FCSTD DOCUMENT  (FreeCAD 1.0R39319 (Git))
Label: Assembly_Launch-Monitor
License: All rights reserved
LicenseURL: https://en.wikipedia.org/wiki/All_rights_reserved
objects: App::Link×37, App::FeaturePython×13, Assembly::AssemblyLink×10, Assembly::JointGroup×1, Assembly::AssemblyObject×1
EXTERNAL_REF file=Assembly_PSU-Stack.FCStd obj=Assembly
EXTERNAL_REF file=Assembly_PSU-Stack.FCStd obj=Stack_Module_PSU
EXTERNAL_REF file=Assembly_PSU-Stack.FCStd obj=Ambient_LED_Screen
EXTERNAL_REF file=Assembly_PSU-Stack.FCStd obj=LinePower_Cover
EXTERNAL_REF file=Assembly_PSU-Stack.FCStd obj=Foot
EXTERNAL_REF file=Assembly_PSU-Stack.FCStd obj=Foot001
EXTERNAL_REF file=Assembly_PSU-Stack.FCStd obj=Foot002
EXTERNAL_REF file=Assembly_PSU-Stack.FCStd obj=Foot003
EXTERNAL_REF file=Assembly_PSU-Stack.FCStd obj=Spacer
EXTERNAL_REF file=Assembly_PSU-Stack.FCStd obj=Spacer001
EXTERNAL_REF file=Assembly_PSU-Stack.FCStd obj=Spacer002
EXTERNAL_REF file=Assembly_PSU-Stack.FCStd obj=Spacer003
EXTERNAL_REF file=Assembly_Flight-Cam-Stack.FCStd obj=Assembly
EXTERNAL_REF file=Assembly_Flight-Cam-Stack.FCStd obj=Stack_Module
EXTERNAL_REF file=Assembly_Flight-Cam-Stack.FCStd obj=Assembly_Flight_Cam_Screen
EXTERNAL_REF file=Assembly_Flight-Cam-Screen.FCStd obj=EyeScreen
EXTERNAL_REF file=Assembly_Flight-Cam-Screen.FCStd obj=EyeScreen_Clamp
EXTERNAL_REF file=Assembly_Flight-Cam-Screen.FCStd obj=Assembly_Flight_Cam
EXTERNAL_REF file=Assembly_Flight-Cam.FCStd obj=IMX296_MPI_Eyeball_6mm001
EXTERNAL_REF file=Assembly_Flight-Cam-Stack.FCStd obj=Spacer
EXTERNAL_REF file=Assembly_Flight-Cam-Stack.FCStd obj=Spacer001
EXTERNAL_REF file=Assembly_Flight-Cam-Stack.FCStd obj=Spacer002
EXTERNAL_REF file=Assembly_Flight-Cam-Stack.FCStd obj=Spacer003
EXTERNAL_REF file=Assembly_LED-Stack.FCStd obj=Assembly
EXTERNAL_REF file=Assembly_LED-Stack.FCStd obj=Stack_Module001
EXTERNAL_REF file=Assembly_LED-Stack.FCStd obj=Assembly_LED_Screen
EXTERNAL_REF file=Assembly_LED-Screen.FCStd obj=EyeScreen001
EXTERNAL_REF file=Assembly_LED-Screen.FCStd obj=Assembly_LED
EXTERNAL_REF file=Assembly_LED.FCStd obj=LED_Eyeball001
EXTERNAL_REF file=Assembly_LED.FCStd obj=LED_Clamp001
EXTERNAL_REF file=Assembly_LED-Screen.FCStd obj=EyeScreen_Clamp001
EXTERNAL_REF file=Assembly_LED-Stack.FCStd obj=Spacer001
EXTERNAL_REF file=Assembly_LED-Stack.FCStd obj=Spacer002
EXTERNAL_REF file=Assembly_LED-Stack.FCStd obj=Spacer003
EXTERNAL_REF file=Assembly_LED-Stack.FCStd obj=Spacer004
EXTERNAL_REF file=Assembly_Tee-Cam-Stack.FCStd obj=Assembly
EXTERNAL_REF file=Assembly_Tee-Cam-Stack.FCStd obj=Stack_Module
EXTERNAL_REF file=Assembly_Tee-Cam-Stack.FCStd obj=Spacer
EXTERNAL_REF file=Assembly_Tee-Cam-Stack.FCStd obj=Spacer001
EXTERNAL_REF file=Assembly_Tee-Cam-Stack.FCStd obj=Spacer002
EXTERNAL_REF file=Assembly_Tee-Cam-Stack.FCStd obj=Spacer003
EXTERNAL_REF file=Assembly_Tee-Cam-Stack.FCStd obj=Assembly_Tee_Cam_Screen
EXTERNAL_REF file=Assembly_Tee-Cam-Screen.FCStd obj=EyeScreen
EXTERNAL_REF file=Assembly_Tee-Cam-Screen.FCStd obj=EyeScreen_Clamp
EXTERNAL_REF file=Assembly_Tee-Cam-Screen.FCStd obj=Assembly_Tee_Cam
EXTERNAL_REF file=Assembly_Tee-Cam.FCStd obj=IMX296_MPI_Eyeball_6mm001
EXTERNAL_REF file=../Part/Print/Stack_Module_Cover.FCStd obj=Part

FEATURE [App::Link] Stack_Module_PSU
  LinkedObject = -> <external Assembly_PSU-Stack.FCStd>#Stack_Module_PSU
FEATURE [App::Link] Ambient_LED_Screen
  LinkPlacement = pos=(-1.22e-14,-3,-62.5) rot=(0,0.707107,-0.707107;3.14159rad)
  LinkedObject = -> <external Assembly_PSU-Stack.FCStd>#Ambient_LED_Screen
  Placement = pos=(-1.22e-14,-3,-62.5) rot=(0,0.707107,-0.707107;3.14159rad)
FEATURE [App::Link] LinePower_Cover
  LinkPlacement = pos=(56,-4,67) rot=(0,-0.707107,0.707107;3.14159rad)
  LinkedObject = -> <external Assembly_PSU-Stack.FCStd>#LinePower_Cover
  Placement = pos=(56,-4,67) rot=(0,-0.707107,0.707107;3.14159rad)
FEATURE [App::Link] Foot
  LinkPlacement = pos=(-66.5,5,-53.5) rot=(0.57735,-0.57735,0.57735;2.0944rad)
  LinkedObject = -> <external Assembly_PSU-Stack.FCStd>#Foot
  Placement = pos=(-66.5,5,-53.5) rot=(0.57735,-0.57735,0.57735;2.0944rad)
FEATURE [App::Link] Foot001
  LinkPlacement = pos=(-63.5,5,62.5) rot=(0.57735,-0.57735,0.57735;2.0944rad)
  LinkedObject = -> <external Assembly_PSU-Stack.FCStd>#Foot001
  Placement = pos=(-63.5,5,62.5) rot=(0.57735,-0.57735,0.57735;2.0944rad)
FEATURE [App::Link] Foot002
  LinkPlacement = pos=(66.5,5,-53.5) rot=(1,0,0;1.5708rad)
  LinkedObject = -> <external Assembly_PSU-Stack.FCStd>#Foot002
  Placement = pos=(66.5,5,-53.5) rot=(1,0,0;1.5708rad)
FEATURE [App::Link] Foot003
  LinkPlacement = pos=(63.5,5,62.5) rot=(0.57735,-0.57735,0.57735;2.0944rad)
  LinkedObject = -> <external Assembly_PSU-Stack.FCStd>#Foot003
  Placement = pos=(63.5,5,62.5) rot=(0.57735,-0.57735,0.57735;2.0944rad)
FEATURE [App::Link] Spacer
  LinkPlacement = pos=(66.5,-35.25,-53.5) rot=(-0.57735,0.57735,-0.57735;4.18879rad)
  LinkedObject = -> <external Assembly_PSU-Stack.FCStd>#Spacer
  Placement = pos=(66.5,-35.25,-53.5) rot=(-0.57735,0.57735,-0.57735;4.18879rad)
FEATURE [App::Link] Spacer001
  LinkPlacement = pos=(63.5,-35.25,62.5) rot=(-0.57735,0.57735,-0.57735;4.18879rad)
  LinkedObject = -> <external Assembly_PSU-Stack.FCStd>#Spacer001
  Placement = pos=(63.5,-35.25,62.5) rot=(-0.57735,0.57735,-0.57735;4.18879rad)
FEATURE [App::Link] Spacer002
  LinkPlacement = pos=(-66.5,-35.25,-53.5) rot=(-0.57735,0.57735,-0.57735;4.18879rad)
  LinkedObject = -> <external Assembly_PSU-Stack.FCStd>#Spacer002
  Placement = pos=(-66.5,-35.25,-53.5) rot=(-0.57735,0.57735,-0.57735;4.18879rad)
FEATURE [App::Link] Spacer003
  LinkPlacement = pos=(-63.5,-35.25,62.5) rot=(0.57735,-0.57735,0.57735;2.0944rad)
  LinkedObject = -> <external Assembly_PSU-Stack.FCStd>#Spacer003
  Placement = pos=(-63.5,-35.25,62.5) rot=(0.57735,-0.57735,0.57735;2.0944rad)
FEATURE [Assembly::AssemblyLink] Assembly_PSU_Stack  label="Assembly_PSU-Stack"
  Group = -> [Stack_Module_PSU,Ambient_LED_Screen,LinePower_Cover,Foot,Foot001,Foot002,Foot003,Spacer,Spacer001,Spacer002,Spacer003]
  LinkedObject = -> <external Assembly_PSU-Stack.FCStd>#Assembly
  Origin = -> Origin001
  Rigid = true
FEATURE [App::FeaturePython] GroundedJoint  # Assembly grounded joint (typed FeaturePython)
  ObjectToGround = -> Assembly_PSU_Stack
FEATURE [App::Link] Stack_Module
  LinkedObject = -> <external Assembly_Flight-Cam-Stack.FCStd>#Stack_Module
FEATURE [App::Link] EyeScreen
  LinkPlacement = pos=(0,0,0) rot=(0,0,1;3.14159rad)
  LinkedObject = -> <external Assembly_Flight-Cam-Screen.FCStd>#EyeScreen
  Placement = pos=(0,0,0) rot=(0,0,1;3.14159rad)
FEATURE [App::Link] EyeScreen_Clamp
  LinkPlacement = pos=(7.31e-14,1.49e-13,-3.757e-13) rot=(0,0,1;0rad)
  LinkedObject = -> <external Assembly_Flight-Cam-Screen.FCStd>#EyeScreen_Clamp
  Placement = pos=(7.31e-14,1.49e-13,-3.757e-13) rot=(0,0,1;0rad)
FEATURE [App::Link] IMX296_MPI_Eyeball_6mm001  label="IMX296-MPI_Eyeball_6mm001"
  LinkedObject = -> <external Assembly_Flight-Cam.FCStd>#IMX296_MPI_Eyeball_6mm001
FEATURE [Assembly::AssemblyLink] Assembly_Flight_Cam  label="Assembly_Flight-Cam"
  Group = -> [IMX296_MPI_Eyeball_6mm001]
  LinkedObject = -> <external Assembly_Flight-Cam-Screen.FCStd>#Assembly_Flight_Cam
  Placement = pos=(9.2e-15,0,0) rot=(0,-1,0;1.5708rad)
  Rigid = true
FEATURE [Assembly::AssemblyLink] Assembly_Flight_Cam_Screen  label="Assembly_Flight-Cam-Screen"
  Group = -> [EyeScreen,EyeScreen_Clamp,Assembly_Flight_Cam]
  LinkedObject = -> <external Assembly_Flight-Cam-Stack.FCStd>#Assembly_Flight_Cam_Screen
  Placement = pos=(-5.33e-14,-44.75,-20) rot=(0.57735,-0.57735,0.57735;2.0944rad)
  Rigid = true
FEATURE [App::Link] Spacer004
  LinkPlacement = pos=(-66.5,-82.5,-53.5) rot=(-0.57735,0.57735,-0.57735;4.18879rad)
  LinkedObject = -> <external Assembly_Flight-Cam-Stack.FCStd>#Spacer
  Placement = pos=(-66.5,-82.5,-53.5) rot=(-0.57735,0.57735,-0.57735;4.18879rad)
FEATURE [App::Link] Spacer005
  LinkPlacement = pos=(63.5,-82.5,62.5) rot=(-0.57735,0.57735,-0.57735;4.18879rad)
  LinkedObject = -> <external Assembly_Flight-Cam-Stack.FCStd>#Spacer001
  Placement = pos=(63.5,-82.5,62.5) rot=(-0.57735,0.57735,-0.57735;4.18879rad)
FEATURE [App::Link] Spacer006
  LinkPlacement = pos=(66.5,-82.5,-53.5) rot=(0.57735,-0.57735,0.57735;2.0944rad)
  LinkedObject = -> <external Assembly_Flight-Cam-Stack.FCStd>#Spacer002
  Placement = pos=(66.5,-82.5,-53.5) rot=(0.57735,-0.57735,0.57735;2.0944rad)
FEATURE [App::Link] Spacer007
  LinkPlacement = pos=(-63.5,-82.5,62.5) rot=(-0.57735,0.57735,-0.57735;4.18879rad)
  LinkedObject = -> <external Assembly_Flight-Cam-Stack.FCStd>#Spacer003
  Placement = pos=(-63.5,-82.5,62.5) rot=(-0.57735,0.57735,-0.57735;4.18879rad)
FEATURE [Assembly::AssemblyLink] Assembly_Flight_Cam_Stack  label="Assembly_Flight-Cam-Stack"
  Group = -> [Stack_Module,Assembly_Flight_Cam_Screen,Spacer004,Spacer005,Spacer006,Spacer007]
  LinkedObject = -> <external Assembly_Flight-Cam-Stack.FCStd>#Assembly
  Origin = -> Origin002
  Placement = pos=(-6.5e-15,-40.25,1.049e-13) rot=(0,0,1;0rad)
  Rigid = true
FEATURE [App::FeaturePython] Joint  label="Distance"  # Assembly joint (typed FeaturePython)
  Activated = true
  AngleMax = 0
  AngleMin = 0
  Detach1 = false
  Detach2 = false
  Distance = 0
  Distance2 = 0
  EnableAngleMax = false
  EnableAngleMin = false
  EnableLengthMax = false
  EnableLengthMin = false
  JointType = 5 (Distance)
  LengthMax = 0
  LengthMin = 0
  Placement1 = pos=(-6.7e-15,3.7e-15,-15.8114) rot=(-0.57735,0.57735,0.57735;2.0944rad)
  Placement2 = pos=(6.38556,-40.25,16.7734) rot=(-0.57735,0.57735,-0.57735;4.18879rad)
  Reference1 = -> Assembly [Assembly_Flight_Cam_Stack.Stack_Module.Body.Face88,Assembly_Flight_Cam_Stack.Stack_Module.Body.Vertex265]
  Reference2 = -> Assembly [Assembly_PSU_Stack.Stack_Module_PSU.Body.Face4,Assembly_PSU_Stack.Stack_Module_PSU.Body.Vertex81]
FEATURE [App::FeaturePython] Joint001  label="Distance001"  # Assembly joint (typed FeaturePython)
  Activated = true
  AngleMax = 0
  AngleMin = 0
  Detach1 = false
  Detach2 = false
  Distance = 0
  Distance2 = 0
  EnableAngleMax = false
  EnableAngleMin = false
  EnableLengthMax = false
  EnableLengthMin = false
  JointType = 5 (Distance)
  LengthMax = 0
  LengthMin = 0
  Placement1 = pos=(59,-20.125,4.65153) rot=(0,-1,0;1.5708rad)
  Placement2 = pos=(59,-43.75,4.65153) rot=(0,-1,0;1.5708rad)
  Reference1 = -> Assembly [Assembly_PSU_Stack.Stack_Module_PSU.Body.Face30,Assembly_PSU_Stack.Stack_Module_PSU.Body.Face30]
  Reference2 = -> Assembly [Assembly_Flight_Cam_Stack.Stack_Module.Body.Face23,Assembly_Flight_Cam_Stack.Stack_Module.Body.Face23]
FEATURE [App::FeaturePython] Joint002  label="Distance002"  # Assembly joint (typed FeaturePython)
  Activated = true
  AngleMax = 0
  AngleMin = 0
  Detach1 = false
  Detach2 = false
  Distance = 0
  Distance2 = 0
  EnableAngleMax = false
  EnableAngleMin = false
  EnableLengthMax = false
  EnableLengthMin = false
  JointType = 5 (Distance)
  LengthMax = 0
  LengthMin = 0
  Placement1 = pos=(-1.62e-14,-10.6176,-70) rot=(0.707107,0.707107,0;3.14159rad)
  Placement2 = pos=(71,-43.75,-70) rot=(-0.57735,-0.57735,0.57735;4.18879rad)
  Reference1 = -> Assembly [Assembly_PSU_Stack.Stack_Module_PSU.Body.Face39,Assembly_PSU_Stack.Stack_Module_PSU.Body.Vertex41]
  Reference2 = -> Assembly [Assembly_Flight_Cam_Stack.Stack_Module.Body.Edge101,Assembly_Flight_Cam_Stack.Stack_Module.Body.Vertex87]
FEATURE [App::Link] Stack_Module001
  LinkedObject = -> <external Assembly_LED-Stack.FCStd>#Stack_Module001
FEATURE [App::Link] EyeScreen001
  LinkedObject = -> <external Assembly_LED-Screen.FCStd>#EyeScreen001
FEATURE [App::Link] LED_Eyeball001
  LinkedObject = -> <external Assembly_LED.FCStd>#LED_Eyeball001
FEATURE [App::Link] LED_Clamp001
  LinkPlacement = pos=(3.8e-15,4.1e-15,-13.35) rot=(0,0,-1;0.785398rad)
  LinkedObject = -> <external Assembly_LED.FCStd>#LED_Clamp001
  Placement = pos=(3.8e-15,4.1e-15,-13.35) rot=(0,0,-1;0.785398rad)
FEATURE [Assembly::AssemblyLink] Assembly_LED
  Group = -> [LED_Eyeball001,LED_Clamp001]
  LinkedObject = -> <external Assembly_LED-Screen.FCStd>#Assembly_LED
  Placement = pos=(-9.2e-15,0,0) rot=(0.678598,0.281085,0.678598;2.59356rad)
  Rigid = true
FEATURE [App::Link] EyeScreen_Clamp001
  LinkPlacement = pos=(-8.42e-14,1.222e-13,2.46e-14) rot=(0,0,1;3.14159rad)
  LinkedObject = -> <external Assembly_LED-Screen.FCStd>#EyeScreen_Clamp001
  Placement = pos=(-8.42e-14,1.222e-13,2.46e-14) rot=(0,0,1;3.14159rad)
FEATURE [Assembly::AssemblyLink] Assembly_LED_Screen  label="Assembly_LED-Screen"
  Group = -> [EyeScreen001,Assembly_LED,EyeScreen_Clamp001]
  LinkedObject = -> <external Assembly_LED-Stack.FCStd>#Assembly_LED_Screen
  Placement = pos=(-2.02e-14,-44.75,-20) rot=(0.57735,0.57735,-0.57735;2.0944rad)
  Rigid = true
FEATURE [App::Link] Spacer008
  LinkPlacement = pos=(63.5,-82.5,62.5) rot=(0.57735,-0.57735,0.57735;2.0944rad)
  LinkedObject = -> <external Assembly_LED-Stack.FCStd>#Spacer001
  Placement = pos=(63.5,-82.5,62.5) rot=(0.57735,-0.57735,0.57735;2.0944rad)
FEATURE [App::Link] Spacer009
  LinkPlacement = pos=(66.5,-82.5,-53.5) rot=(-0.57735,0.57735,-0.57735;4.18879rad)
  LinkedObject = -> <external Assembly_LED-Stack.FCStd>#Spacer002
  Placement = pos=(66.5,-82.5,-53.5) rot=(-0.57735,0.57735,-0.57735;4.18879rad)
FEATURE [App::Link] Spacer010
  LinkPlacement = pos=(-66.5,-82.5,-53.5) rot=(-0.57735,0.57735,-0.57735;4.18879rad)
  LinkedObject = -> <external Assembly_LED-Stack.FCStd>#Spacer003
  Placement = pos=(-66.5,-82.5,-53.5) rot=(-0.57735,0.57735,-0.57735;4.18879rad)
FEATURE [App::Link] Spacer011
  LinkPlacement = pos=(-63.5,-82.5,62.5) rot=(-0.57735,0.57735,-0.57735;4.18879rad)
  LinkedObject = -> <external Assembly_LED-Stack.FCStd>#Spacer004
  Placement = pos=(-63.5,-82.5,62.5) rot=(-0.57735,0.57735,-0.57735;4.18879rad)
FEATURE [Assembly::AssemblyLink] Assembly_LED_Stack  label="Assembly_LED-Stack"
  Group = -> [Stack_Module001,Assembly_LED_Screen,Spacer008,Spacer009,Spacer010,Spacer011]
  LinkedObject = -> <external Assembly_LED-Stack.FCStd>#Assembly
  Origin = -> Origin003
  Placement = pos=(-8.5e-15,-127.75,1.504e-13) rot=(0,0,1;0rad)
  Rigid = true
FEATURE [App::FeaturePython] Joint003  label="Distance003"  # Assembly joint (typed FeaturePython)
  Activated = true
  AngleMax = 0
  AngleMin = 0
  Detach1 = false
  Detach2 = false
  Distance = 0
  Distance2 = 0
  EnableAngleMax = false
  EnableAngleMin = false
  EnableLengthMax = false
  EnableLengthMin = false
  JointType = 5 (Distance)
  LengthMax = 0
  LengthMin = 0
  Placement1 = pos=(-6.7e-15,3.7e-15,-15.8114) rot=(-0.57735,0.57735,0.57735;2.0944rad)
  Placement2 = pos=(57.7645,-87.5,-3.95134) rot=(0.57735,-0.57735,0.57735;2.0944rad)
  Reference1 = -> Assembly [Assembly_LED_Stack.Stack_Module001.Face88,Assembly_LED_Stack.Stack_Module001.Vertex296]
  Reference2 = -> Assembly [Assembly_Flight_Cam_Stack.Stack_Module.Body.Face52,Assembly_Flight_Cam_Stack.Stack_Module.Body.Vertex174]
FEATURE [App::FeaturePython] Joint004  label="Distance004"  # Assembly joint (typed FeaturePython)
  Activated = true
  AngleMax = 0
  AngleMin = 0
  Detach1 = false
  Detach2 = false
  Distance = 0
  Distance2 = 0
  EnableAngleMax = false
  EnableAngleMin = false
  EnableLengthMax = false
  EnableLengthMin = false
  JointType = 5 (Distance)
  LengthMax = 0
  LengthMin = 0
  Placement1 = pos=(59,-43.75,4.65153) rot=(0,-1,0;1.5708rad)
  Placement2 = pos=(59,-43.75,4.65153) rot=(0,-1,0;1.5708rad)
  Reference1 = -> Assembly [Assembly_LED_Stack.Stack_Module001.Face23,Assembly_LED_Stack.Stack_Module001.Face23]
  Reference2 = -> Assembly [Assembly_Flight_Cam_Stack.Stack_Module.Body.Face23,Assembly_Flight_Cam_Stack.Stack_Module.Body.Face23]
FEATURE [App::FeaturePython] Joint005  label="Distance005"  # Assembly joint (typed FeaturePython)
  Activated = true
  AngleMax = 0
  AngleMin = 0
  Detach1 = false
  Detach2 = false
  Distance = 0
  Distance2 = 0
  EnableAngleMax = false
  EnableAngleMin = false
  EnableLengthMax = false
  EnableLengthMin = false
  JointType = 5 (Distance)
  LengthMax = 0
  LengthMin = 0
  Placement1 = pos=(68,-43.75,-70) rot=(0,0,1;0rad)
  Placement2 = pos=(68,-43.75,-70) rot=(0,0,1;0rad)
  Reference1 = -> Assembly [Assembly_LED_Stack.Stack_Module001.Face15,Assembly_LED_Stack.Stack_Module001.Vertex88]
  Reference2 = -> Assembly [Assembly_Flight_Cam_Stack.Stack_Module.Body.Face15,Assembly_Flight_Cam_Stack.Stack_Module.Body.Vertex90]
FEATURE [App::Link] Stack_Module002
  LinkedObject = -> <external Assembly_Tee-Cam-Stack.FCStd>#Stack_Module
FEATURE [App::Link] Spacer012
  LinkPlacement = pos=(-66.5,-82.5,-53.5) rot=(-0.57735,0.57735,-0.57735;4.18879rad)
  LinkedObject = -> <external Assembly_Tee-Cam-Stack.FCStd>#Spacer
  Placement = pos=(-66.5,-82.5,-53.5) rot=(-0.57735,0.57735,-0.57735;4.18879rad)
FEATURE [App::Link] Spacer013
  LinkPlacement = pos=(63.5,-82.5,62.5) rot=(0.57735,-0.57735,0.57735;2.0944rad)
  LinkedObject = -> <external Assembly_Tee-Cam-Stack.FCStd>#Spacer001
  Placement = pos=(63.5,-82.5,62.5) rot=(0.57735,-0.57735,0.57735;2.0944rad)
FEATURE [App::Link] Spacer014
  LinkPlacement = pos=(66.5,-82.5,-53.5) rot=(0.57735,-0.57735,0.57735;2.0944rad)
  LinkedObject = -> <external Assembly_Tee-Cam-Stack.FCStd>#Spacer002
  Placement = pos=(66.5,-82.5,-53.5) rot=(0.57735,-0.57735,0.57735;2.0944rad)
FEATURE [App::Link] Spacer015
  LinkPlacement = pos=(-63.5,-82.5,62.5) rot=(-0.57735,0.57735,-0.57735;4.18879rad)
  LinkedObject = -> <external Assembly_Tee-Cam-Stack.FCStd>#Spacer003
  Placement = pos=(-63.5,-82.5,62.5) rot=(-0.57735,0.57735,-0.57735;4.18879rad)
FEATURE [App::Link] EyeScreen002
  LinkPlacement = pos=(0,0,0) rot=(0,0,1;3.14159rad)
  LinkedObject = -> <external Assembly_Tee-Cam-Screen.FCStd>#EyeScreen
  Placement = pos=(0,0,0) rot=(0,0,1;3.14159rad)
FEATURE [App::Link] EyeScreen_Clamp002
  LinkPlacement = pos=(6.2e-14,1.473e-13,-3.4e-13) rot=(0,0,1;0rad)
  LinkedObject = -> <external Assembly_Tee-Cam-Screen.FCStd>#EyeScreen_Clamp
  Placement = pos=(6.2e-14,1.473e-13,-3.4e-13) rot=(0,0,1;0rad)
FEATURE [App::Link] IMX296_MPI_Eyeball_6mm002  label="IMX296-MPI_Eyeball_6mm002"
  LinkedObject = -> <external Assembly_Tee-Cam.FCStd>#IMX296_MPI_Eyeball_6mm001
FEATURE [Assembly::AssemblyLink] Assembly_Tee_Cam  label="Assembly_Tee-Cam"
  Group = -> [IMX296_MPI_Eyeball_6mm002]
  LinkedObject = -> <external Assembly_Tee-Cam-Screen.FCStd>#Assembly_Tee_Cam
  Placement = pos=(9.2e-15,0,0) rot=(0.57735,0.57735,-0.57735;4.18879rad)
  Rigid = true
FEATURE [Assembly::AssemblyLink] Assembly_Tee_Cam_Screen  label="Assembly_Tee-Cam-Screen"
  Group = -> [EyeScreen002,EyeScreen_Clamp002,Assembly_Tee_Cam]
  LinkedObject = -> <external Assembly_Tee-Cam-Stack.FCStd>#Assembly_Tee_Cam_Screen
  Placement = pos=(1,-44.75,-20) rot=(-0.57735,0.57735,-0.57735;4.18879rad)
  Rigid = true
FEATURE [Assembly::AssemblyLink] Assembly_Tee_Cam_Stack  label="Assembly_Tee-Cam-Stack"
  Group = -> [Stack_Module002,Spacer012,Spacer013,Spacer014,Spacer015,Assembly_Tee_Cam_Screen]
  LinkedObject = -> <external Assembly_Tee-Cam-Stack.FCStd>#Assembly
  Origin = -> Origin004
  Placement = pos=(-2.32e-14,-215.25,1.736e-13) rot=(0,0,1;0rad)
  Rigid = true
FEATURE [App::FeaturePython] Joint006  label="Distance006"  # Assembly joint (typed FeaturePython)
  Activated = true
  AngleMax = 0
  AngleMin = 0
  Detach1 = false
  Detach2 = false
  Distance = 0
  Distance2 = 0
  EnableAngleMax = false
  EnableAngleMin = false
  EnableLengthMax = false
  EnableLengthMin = false
  JointType = 5 (Distance)
  LengthMax = 0
  LengthMin = 0
  Placement1 = pos=(-6.7e-15,3.7e-15,-15.8114) rot=(-0.57735,0.57735,0.57735;2.0944rad)
  Placement2 = pos=(-57.7645,-87.5,-3.95134) rot=(0.57735,0.57735,0.57735;4.18879rad)
  Reference1 = -> Assembly [Assembly_Tee_Cam_Stack.Stack_Module002.Body.Face88,Assembly_Tee_Cam_Stack.Stack_Module002.Body.Vertex258]
  Reference2 = -> Assembly [Assembly_LED_Stack.Stack_Module001.Face131,Assembly_LED_Stack.Stack_Module001.Vertex351]
FEATURE [App::FeaturePython] Joint007  label="Distance007"  # Assembly joint (typed FeaturePython)
  Activated = true
  AngleMax = 0
  AngleMin = 0
  Detach1 = false
  Detach2 = false
  Distance = 0
  Distance2 = 0
  EnableAngleMax = false
  EnableAngleMin = false
  EnableLengthMax = false
  EnableLengthMin = false
  JointType = 5 (Distance)
  LengthMax = 0
  LengthMin = 0
  Placement1 = pos=(59,-43.75,4.65153) rot=(0,-1,0;1.5708rad)
  Placement2 = pos=(59,-43.75,4.65153) rot=(0,-1,0;1.5708rad)
  Reference1 = -> Assembly [Assembly_Tee_Cam_Stack.Stack_Module002.Body.Face23,Assembly_Tee_Cam_Stack.Stack_Module002.Body.Face23]
  Reference2 = -> Assembly [Assembly_LED_Stack.Stack_Module001.Face23,Assembly_LED_Stack.Stack_Module001.Face23]
FEATURE [App::FeaturePython] Joint008  label="Distance008"  # Assembly joint (typed FeaturePython)
  Activated = true
  AngleMax = 0
  AngleMin = 0
  Detach1 = false
  Detach2 = false
  Distance = 0
  Distance2 = 0
  EnableAngleMax = false
  EnableAngleMin = false
  EnableLengthMax = false
  EnableLengthMin = false
  JointType = 5 (Distance)
  LengthMax = 0
  LengthMin = 0
  Placement1 = pos=(68,-43.75,-70) rot=(0,0,1;0rad)
  Placement2 = pos=(68,-43.75,-70) rot=(0,0,1;0rad)
  Reference1 = -> Assembly [Assembly_Tee_Cam_Stack.Stack_Module002.Body.Face15,Assembly_Tee_Cam_Stack.Stack_Module002.Body.Face15]
  Reference2 = -> Assembly [Assembly_LED_Stack.Stack_Module001.Face15,Assembly_LED_Stack.Stack_Module001.Vertex90]
FEATURE [App::Link] Stack_Module_Cover
  LinkPlacement = pos=(-5.16e-14,-302.75,3.692e-13) rot=(0,0,1;0rad)
  LinkedObject = -> <external ../Part/Print/Stack_Module_Cover.FCStd>#Part
  Placement = pos=(-5.16e-14,-302.75,3.692e-13) rot=(0,0,1;0rad)
FEATURE [App::FeaturePython] Joint009  label="Distance009"  # Assembly joint (typed FeaturePython)
  Activated = true
  AngleMax = 0
  AngleMin = 0
  Detach1 = false
  Detach2 = false
  Distance = 0
  Distance2 = 0
  EnableAngleMax = false
  EnableAngleMin = false
  EnableLengthMax = false
  EnableLengthMin = false
  JointType = 5 (Distance)
  LengthMax = 0
  LengthMin = 0
  Placement1 = pos=(-1.02e-14,8.7e-15,13.4612) rot=(-0.57735,0.57735,0.57735;2.0944rad)
  Placement2 = pos=(57.7645,-87.5,-3.95134) rot=(0.57735,-0.57735,0.57735;2.0944rad)
  Reference1 = -> Assembly [Stack_Module_Cover.Body.Face2,Stack_Module_Cover.Body.Vertex34]
  Reference2 = -> Assembly [Assembly_Tee_Cam_Stack.Stack_Module002.Body.Face52,Assembly_Tee_Cam_Stack.Stack_Module002.Body.Vertex174]
FEATURE [App::FeaturePython] Joint010  label="Distance010"  # Assembly joint (typed FeaturePython)
  Activated = true
  AngleMax = 0
  AngleMin = 0
  Detach1 = false
  Detach2 = false
  Distance = 0
  Distance2 = 0
  EnableAngleMax = false
  EnableAngleMin = false
  EnableLengthMax = false
  EnableLengthMin = false
  JointType = 5 (Distance)
  LengthMax = 0
  LengthMin = 0
  Placement1 = pos=(59,-5,4.65153) rot=(0,-1,0;1.5708rad)
  Placement2 = pos=(59,-43.75,4.65153) rot=(0,-1,0;1.5708rad)
  Reference1 = -> Assembly [Stack_Module_Cover.Body.Face16,Stack_Module_Cover.Body.Face16]
  Reference2 = -> Assembly [Assembly_Tee_Cam_Stack.Stack_Module002.Body.Face23,Assembly_Tee_Cam_Stack.Stack_Module002.Body.Face23]
FEATURE [App::FeaturePython] Joint011  label="Distance011"  # Assembly joint (typed FeaturePython)
  Activated = true
  AngleMax = 0
  AngleMin = 0
  Detach1 = false
  Detach2 = false
  Distance = 0
  Distance2 = 0
  EnableAngleMax = false
  EnableAngleMin = false
  EnableLengthMax = false
  EnableLengthMin = false
  JointType = 5 (Distance)
  LengthMax = 0
  LengthMin = 0
  Placement1 = pos=(0,-5.70149,-70) rot=(0.707107,0.707107,0;3.14159rad)
  Placement2 = pos=(68,-43.75,-70) rot=(0,0,1;0rad)
  Reference1 = -> Assembly [Stack_Module_Cover.Body.Face5,Stack_Module_Cover.Body.Vertex45]
  Reference2 = -> Assembly [Assembly_Tee_Cam_Stack.Stack_Module002.Body.Face15,Assembly_Tee_Cam_Stack.Stack_Module002.Body.Vertex90]
FEATURE [Assembly::JointGroup] Joints
  Group = -> [GroundedJoint,Joint,Joint001,Joint002,Joint003,Joint004,Joint005,Joint006,Joint007,Joint008,Joint009,Joint010,Joint011]
FEATURE [Assembly::AssemblyObject] Assembly  label="Assembly_Launch-Monitor"
  Group = -> [Joints,Assembly_PSU_Stack,GroundedJoint,Assembly_Flight_Cam_Stack,Joint,Joint001,Joint002,Assembly_LED_Stack,Joint003,Joint004,Joint005,Assembly_Tee_Cam_Stack,Joint006,Joint007,Joint008,Stack_Module_Cover,Joint009,Joint010,Joint011]
  Origin = -> Origin
  Type = Assembly

RESOLVED EXTERNAL PARTS (link-assembly join: the EXTERNAL_REF files above that resolve inside this repo's crawl, each included once):
---- part Assembly_Flight-Cam-Screen.FCStd = doc fcstd_e77e65b90301 ----
FCSTD DOCUMENT  (FreeCAD 1.0R39319 (Git))
Label: Assembly_Flight-Cam-Screen
License: All rights reserved
LicenseURL: https://en.wikipedia.org/wiki/All_rights_reserved
objects: App::FeaturePython×5, App::Link×3, Assembly::AssemblyLink×1, Assembly::JointGroup×1, Assembly::AssemblyObject×1
EXTERNAL_REF file=../Part/Print/EyeScreen.FCStd obj=Part
EXTERNAL_REF file=../Part/Print/EyeScreen_Clamp.FCStd obj=Part
EXTERNAL_REF file=Assembly_Flight-Cam.FCStd obj=Assembly
EXTERNAL_REF file=Assembly_Flight-Cam.FCStd obj=IMX296_MPI_Eyeball_6mm001

FEATURE [App::Link] EyeScreen
  LinkPlacement = pos=(0,0,0) rot=(0,0,1;3.14159rad)
  LinkedObject = -> <external ../Part/Print/EyeScreen.FCStd>#Part
  Placement = pos=(0,0,0) rot=(0,0,1;3.14159rad)
FEATURE [App::Link] EyeScreen_Clamp
  LinkPlacement = pos=(6.23e-14,1.5e-13,-2.196e-13) rot=(0,0,1;0rad)
  LinkedObject = -> <external ../Part/Print/EyeScreen_Clamp.FCStd>#Part
  Placement = pos=(6.23e-14,1.5e-13,-2.196e-13) rot=(0,0,1;0rad)
FEATURE [App::FeaturePython] GroundedJoint  # Assembly grounded joint (typed FeaturePython)
  ObjectToGround = -> EyeScreen
FEATURE [App::FeaturePython] Joint  label="Distance"  # Assembly joint (typed FeaturePython)
  Activated = true
  AngleMax = 0
  AngleMin = 0
  Detach1 = false
  Detach2 = false
  Distance = -1
  Distance2 = 0
  EnableAngleMax = false
  EnableAngleMin = false
  EnableLengthMax = false
  EnableLengthMin = false
  JointType = 5 (Distance)
  LengthMax = 0
  LengthMin = 0
  Placement1 = pos=(1,-2.077e-13,-1.63309) rot=(0.707107,0,0.707107;3.14159rad)
  Placement2 = pos=(4.82e-14,-4.807e-13,-1.66411) rot=(0.707107,0,-0.707107;3.14159rad)
  Reference1 = -> Assembly [EyeScreen_Clamp.Body.Face3,EyeScreen_Clamp.Body.Edge29]
  Reference2 = -> Assembly [EyeScreen.Body.Face105,EyeScreen.Body.Vertex111]
FEATURE [App::FeaturePython] Joint001  label="Cylindrical"  # Assembly joint (typed FeaturePython)
  Activated = true
  AngleMax = 0
  AngleMin = 0
  Detach1 = false
  Detach2 = false
  Distance = 0
  Distance2 = 0
  EnableAngleMax = false
  EnableAngleMin = false
  EnableLengthMax = false
  EnableLengthMin = false
  JointType = 2 (Cylindrical)
  LengthMax = 0
  LengthMin = 0
  Placement1 = pos=(3,-43.3013,25) rot=(0.57735,-0.57735,-0.57735;2.0944rad)
  Placement2 = pos=(5,43.3013,25) rot=(0.57735,0.57735,0.57735;2.0944rad)
  Reference1 = -> Assembly [EyeScreen_Clamp.Body.Face32,EyeScreen_Clamp.Body.Face32]
  Reference2 = -> Assembly [EyeScreen.Body.Face28,EyeScreen.Body.Face28]
FEATURE [App::FeaturePython] Joint002  label="Cylindrical001"  # Assembly joint (typed FeaturePython)
  Activated = true
  AngleMax = 0
  AngleMin = 0
  Detach1 = false
  Detach2 = false
  Distance = 0
  Distance2 = 0
  EnableAngleMax = false
  EnableAngleMin = false
  EnableLengthMax = false
  EnableLengthMin = false
  JointType = 2 (Cylindrical)
  LengthMax = 0
  LengthMin = 0
  Placement1 = pos=(3,-43.3013,-25) rot=(0.57735,-0.57735,0.57735;4.18879rad)
  Placement2 = pos=(5,43.3013,-25) rot=(0.57735,0.57735,-0.57735;4.18879rad)
  Reference1 = -> Assembly [EyeScreen_Clamp.Body.Face31,EyeScreen_Clamp.Body.Face31]
  Reference2 = -> Assembly [EyeScreen.Body.Face29,EyeScreen.Body.Face29]
FEATURE [App::Link] IMX296_MPI_Eyeball_6mm001  label="IMX296-MPI_Eyeball_6mm001"
  LinkedObject = -> <external Assembly_Flight-Cam.FCStd>#IMX296_MPI_Eyeball_6mm001
FEATURE [Assembly::AssemblyLink] Assembly_Flight_Cam  label="Assembly_Flight-Cam"
  Group = -> [IMX296_MPI_Eyeball_6mm001]
  LinkedObject = -> <external Assembly_Flight-Cam.FCStd>#Assembly
  Origin = -> Origin001
  Placement = pos=(9.2e-15,0,0) rot=(0,-1,0;1.5708rad)
  Rigid = true
FEATURE [App::FeaturePython] Joint003  label="Ball"  # Assembly joint (typed FeaturePython)
  Activated = true
  AngleMax = 0
  AngleMin = 0
  Detach1 = false
  Detach2 = false
  Distance = 0
  Distance2 = 0
  EnableAngleMax = false
  EnableAngleMin = false
  EnableLengthMax = false
  EnableLengthMin = false
  JointType = 4 (Ball)
  LengthMax = 0
  LengthMin = 0
  Placement1 = pos=(0,0,0) rot=(1,0,0;3.14159rad)
  Placement2 = pos=(-9.2e-15,0,0) rot=(0.707107,0,0.707107;3.14159rad)
  Reference1 = -> Assembly [Assembly_Flight_Cam.IMX296_MPI_Eyeball_6mm001.Face1,Assembly_Flight_Cam.IMX296_MPI_Eyeball_6mm001.Face1]
  Reference2 = -> Assembly [EyeScreen.Body.Edge142,EyeScreen.Body.Edge142]
FEATURE [Assembly::JointGroup] Joints
  Group = -> [GroundedJoint,Joint,Joint001,Joint002,Joint003]
FEATURE [Assembly::AssemblyObject] Assembly  label="Assembly_Flight-Cam-Screen"
  Group = -> [Joints,EyeScreen,EyeScreen_Clamp,GroundedJoint,Joint,Joint001,Joint002,Assembly_Flight_Cam,Joint003]
  Origin = -> Origin
  Type = Assembly_Flight-Cam-Screen
---- part Assembly_Flight-Cam-Stack.FCStd = doc fcstd_b05a0b03a1ce ----
FCSTD DOCUMENT  (FreeCAD 1.0R39319 (Git))
Label: Assembly_Flight-Cam-Stack
License: All rights reserved
LicenseURL: https://en.wikipedia.org/wiki/All_rights_reserved
objects: App::FeaturePython×12, App::Link×8, Assembly::AssemblyLink×2, Assembly::JointGroup×1, Assembly::AssemblyObject×1
EXTERNAL_REF file=../Part/Print/Stack_Module.FCStd obj=Part
EXTERNAL_REF file=Assembly_Flight-Cam-Screen.FCStd obj=Assembly
EXTERNAL_REF file=Assembly_Flight-Cam-Screen.FCStd obj=EyeScreen
EXTERNAL_REF file=Assembly_Flight-Cam-Screen.FCStd obj=EyeScreen_Clamp
EXTERNAL_REF file=Assembly_Flight-Cam-Screen.FCStd obj=Assembly_Flight_Cam
EXTERNAL_REF file=Assembly_Flight-Cam.FCStd obj=IMX296_MPI_Eyeball_6mm001
EXTERNAL_REF file=../Part/Print/Spacer.FCStd obj=Part

FEATURE [App::Link] Stack_Module
  LinkedObject = -> <external ../Part/Print/Stack_Module.FCStd>#Part
FEATURE [App::FeaturePython] GroundedJoint  # Assembly grounded joint (typed FeaturePython)
  ObjectToGround = -> Stack_Module
FEATURE [App::Link] EyeScreen
  LinkPlacement = pos=(0,0,0) rot=(0,0,1;3.14159rad)
  LinkedObject = -> <external Assembly_Flight-Cam-Screen.FCStd>#EyeScreen
  Placement = pos=(0,0,0) rot=(0,0,1;3.14159rad)
FEATURE [App::Link] EyeScreen_Clamp
  LinkPlacement = pos=(6.23e-14,1.5e-13,-2.196e-13) rot=(0,0,1;0rad)
  LinkedObject = -> <external Assembly_Flight-Cam-Screen.FCStd>#EyeScreen_Clamp
  Placement = pos=(6.23e-14,1.5e-13,-2.196e-13) rot=(0,0,1;0rad)
FEATURE [App::Link] IMX296_MPI_Eyeball_6mm001  label="IMX296-MPI_Eyeball_6mm001"
  LinkedObject = -> <external Assembly_Flight-Cam.FCStd>#IMX296_MPI_Eyeball_6mm001
FEATURE [Assembly::AssemblyLink] Assembly_Flight_Cam  label="Assembly_Flight-Cam"
  Group = -> [IMX296_MPI_Eyeball_6mm001]
  LinkedObject = -> <external Assembly_Flight-Cam-Screen.FCStd>#Assembly_Flight_Cam
  Placement = pos=(9.2e-15,0,0) rot=(0,-1,0;1.5708rad)
  Rigid = true
FEATURE [Assembly::AssemblyLink] Assembly_Flight_Cam_Screen  label="Assembly_Flight-Cam-Screen"
  Group = -> [EyeScreen,EyeScreen_Clamp,Assembly_Flight_Cam]
  LinkedObject = -> <external Assembly_Flight-Cam-Screen.FCStd>#Assembly
  Origin = -> Origin001
  Placement = pos=(-5.71e-14,-44.75,-20) rot=(0.57735,-0.57735,0.57735;2.0944rad)
  Rigid = true
FEATURE [App::FeaturePython] Joint  label="Distance"  # Assembly joint (typed FeaturePython)
  Activated = true
  AngleMax = 0
  AngleMin = 0
  Detach1 = false
  Detach2 = false
  Distance = 0
  Distance2 = 0
  EnableAngleMax = false
  EnableAngleMin = false
  EnableLengthMax = false
  EnableLengthMin = false
  JointType = 5 (Distance)
  LengthMax = 0
  LengthMin = 0
  Placement1 = pos=(7.67986,-2.327e-13,-41.75) rot=(0,1,0;3.14159rad)
  Placement2 = pos=(-4.4e-15,-3,-23.9856) rot=(0.57735,-0.57735,0.57735;2.0944rad)
  Reference1 = -> Assembly [Assembly_Flight_Cam_Screen.EyeScreen.Body.Face97,Assembly_Flight_Cam_Screen.EyeScreen.Body.Vertex133]
  Reference2 = -> Assembly [Stack_Module.Body.Face6,Stack_Module.Body.Vertex58]
FEATURE [App::FeaturePython] Joint001  label="Distance001"  # Assembly joint (typed FeaturePython)
  Activated = true
  AngleMax = 0
  AngleMin = 0
  Detach1 = false
  Detach2 = false
  Distance = -30
  Distance2 = 0
  EnableAngleMax = false
  EnableAngleMin = false
  EnableLengthMax = false
  EnableLengthMin = false
  JointType = 5 (Distance)
  LengthMax = 0
  LengthMin = 0
  Placement1 = pos=(7.6e-15,-40.4281,-60) rot=(0.707107,0.707107,0;3.14159rad)
  Placement2 = pos=(10,-40.7934,-1.63012) rot=(0,-1,0;1.5708rad)
  Reference1 = -> Assembly [Stack_Module.Body.Face206,Stack_Module.Body.Vertex218]
  Reference2 = -> Assembly [Assembly_Flight_Cam_Screen.EyeScreen.Body.Face2,Assembly_Flight_Cam_Screen.EyeScreen.Body.Edge30]
FEATURE [App::FeaturePython] Joint002  label="Distance002"  # Assembly joint (typed FeaturePython)
  Activated = true
  AngleMax = 0
  AngleMin = 0
  Detach1 = false
  Detach2 = false
  Distance = 1
  Distance2 = 0
  EnableAngleMax = false
  EnableAngleMin = false
  EnableLengthMax = false
  EnableLengthMin = false
  JointType = 5 (Distance)
  LengthMax = 0
  LengthMin = 0
  Placement1 = pos=(56,-43.2991,-15.4982) rot=(-0.707107,0,0.707107;3.14159rad)
  Placement2 = pos=(10,55,-3.5) rot=(0,0,1;0rad)
  Reference1 = -> Assembly [Stack_Module.Body.Face53,Stack_Module.Body.Vertex84]
  Reference2 = -> Assembly [Assembly_Flight_Cam_Screen.EyeScreen.Body.Edge63,Assembly_Flight_Cam_Screen.EyeScreen.Body.Edge63]
FEATURE [App::Link] Spacer
  LinkPlacement = pos=(-66.5,-82.5,-53.5) rot=(-0.57735,0.57735,-0.57735;4.18879rad)
  LinkedObject = -> <external ../Part/Print/Spacer.FCStd>#Part
  Placement = pos=(-66.5,-82.5,-53.5) rot=(-0.57735,0.57735,-0.57735;4.18879rad)
FEATURE [App::Link] Spacer001
  LinkPlacement = pos=(63.5,-82.5,62.5) rot=(-0.57735,0.57735,-0.57735;4.18879rad)
  LinkedObject = -> <external ../Part/Print/Spacer.FCStd>#Part
  Placement = pos=(63.5,-82.5,62.5) rot=(-0.57735,0.57735,-0.57735;4.18879rad)
FEATURE [App::Link] Spacer002
  LinkPlacement = pos=(66.5,-82.5,-53.5) rot=(0.57735,-0.57735,0.57735;2.0944rad)
  LinkedObject = -> <external ../Part/Print/Spacer.FCStd>#Part
  Placement = pos=(66.5,-82.5,-53.5) rot=(0.57735,-0.57735,0.57735;2.0944rad)
FEATURE [App::Link] Spacer003
  LinkPlacement = pos=(-63.5,-82.5,62.5) rot=(-0.57735,0.57735,-0.57735;4.18879rad)
  LinkedObject = -> <external ../Part/Print/Spacer.FCStd>#Part
  Placement = pos=(-63.5,-82.5,62.5) rot=(-0.57735,0.57735,-0.57735;4.18879rad)
FEATURE [App::FeaturePython] Joint003  label="Distance003"  # Assembly joint (typed FeaturePython)
  Activated = true
  AngleMax = 0
  AngleMin = 0
  Detach1 = false
  Detach2 = false
  Distance = 0
  Distance2 = 0
  EnableAngleMax = false
  EnableAngleMin = false
  EnableLengthMax = false
  EnableLengthMin = false
  JointType = 5 (Distance)
  LengthMax = 0
  LengthMin = 0
  Placement1 = pos=(-3.1e-15,-9e-16,0) rot=(0,0,1;0rad)
  Placement2 = pos=(63.5,-82.5,62.5) rot=(0.57735,0.57735,0.57735;4.18879rad)
  Reference1 = -> Assembly [Spacer001.Body.Face4,Spacer001.Body.Face4]
  Reference2 = -> Assembly [Stack_Module.Body.Face84,Stack_Module.Body.Edge2]
FEATURE [App::FeaturePython] Joint004  label="Cylindrical"  # Assembly joint (typed FeaturePython)
  Activated = true
  AngleMax = 0
  AngleMin = 0
  Detach1 = false
  Detach2 = false
  Distance = 0
  Distance2 = 0
  EnableAngleMax = false
  EnableAngleMin = false
  EnableLengthMax = false
  EnableLengthMin = false
  JointType = 2 (Cylindrical)
  LengthMax = 0
  LengthMin = 0
  Placement1 = pos=(0,0,3.5) rot=(0,0,1;0rad)
  Placement2 = pos=(63.5,-85,62.5) rot=(1,0,0;1.5708rad)
  Reference1 = -> Assembly [Spacer001.Body.Face1,Spacer001.Body.Face1]
  Reference2 = -> Assembly [Stack_Module.Body.Face69,Stack_Module.Body.Face69]
FEATURE [App::FeaturePython] Joint005  label="Distance004"  # Assembly joint (typed FeaturePython)
  Activated = true
  AngleMax = 0
  AngleMin = 0
  Detach1 = false
  Detach2 = false
  Distance = 0
  Distance2 = 0
  EnableAngleMax = false
  EnableAngleMin = false
  EnableLengthMax = false
  EnableLengthMin = false
  JointType = 5 (Distance)
  LengthMax = 0
  LengthMin = 0
  Placement1 = pos=(-3.1e-15,-9e-16,0) rot=(0,0,1;0rad)
  Placement2 = pos=(66.5,-82.5,-53.5) rot=(0.57735,0.57735,0.57735;4.18879rad)
  Reference1 = -> Assembly [Spacer002.Body.Face4,Spacer002.Body.Face4]
  Reference2 = -> Assembly [Stack_Module.Body.Face80,Stack_Module.Body.Edge2]
FEATURE [App::FeaturePython] Joint006  label="Cylindrical001"  # Assembly joint (typed FeaturePython)
  Activated = true
  AngleMax = 0
  AngleMin = 0
  Detach1 = false
  Detach2 = false
  Distance = 0
  Distance2 = 0
  EnableAngleMax = false
  EnableAngleMin = false
  EnableLengthMax = false
  EnableLengthMin = false
  JointType = 2 (Cylindrical)
  LengthMax = 0
  LengthMin = 0
  Placement1 = pos=(0,0,3.5) rot=(0,0,1;0rad)
  Placement2 = pos=(66.5,-85,-53.5) rot=(1,0,0;1.5708rad)
  Reference1 = -> Assembly [Spacer002.Body.Face1,Spacer002.Body.Face1]
  Reference2 = -> Assembly [Stack_Module.Body.Face68,Stack_Module.Body.Face68]
FEATURE [App::FeaturePython] Joint007  label="Distance005"  # Assembly joint (typed FeaturePython)
  Activated = true
  AngleMax = 0
  AngleMin = 0
  Detach1 = false
  Detach2 = false
  Distance = 0
  Distance2 = 0
  EnableAngleMax = false
  EnableAngleMin = false
  EnableLengthMax = false
  EnableLengthMin = false
  JointType = 5 (Distance)
  LengthMax = 0
  LengthMin = 0
  Placement1 = pos=(-3.1e-15,-9e-16,0) rot=(0,0,1;0rad)
  Placement2 = pos=(-66.5,-82.5,-53.5) rot=(0.57735,-0.57735,0.57735;2.0944rad)
  Reference1 = -> Assembly [Spacer.Body.Face4,Spacer.Body.Vertex5]
  Reference2 = -> Assembly [Stack_Module.Body.Face162,Stack_Module.Body.Edge2]
FEATURE [App::FeaturePython] Joint008  label="Cylindrical002"  # Assembly joint (typed FeaturePython)
  Activated = true
  AngleMax = 0
  AngleMin = 0
  Detach1 = false
  Detach2 = false
  Distance = 0
  Distance2 = 0
  EnableAngleMax = false
  EnableAngleMin = false
  EnableLengthMax = false
  EnableLengthMin = false
  JointType = 2 (Cylindrical)
  LengthMax = 0
  LengthMin = 0
  Placement1 = pos=(0,0,3.5) rot=(0,0,1;0rad)
  Placement2 = pos=(-66.5,-85,-53.5) rot=(0,0.707107,0.707107;3.14159rad)
  Reference1 = -> Assembly [Spacer.Body.Face1,Spacer.Body.Face1]
  Reference2 = -> Assembly [Stack_Module.Body.Face158,Stack_Module.Body.Face158]
FEATURE [App::FeaturePython] Joint009  label="Distance006"  # Assembly joint (typed FeaturePython)
  Activated = true
  AngleMax = 0
  AngleMin = 0
  Detach1 = false
  Detach2 = false
  Distance = 0
  Distance2 = 0
  EnableAngleMax = false
  EnableAngleMin = false
  EnableLengthMax = false
  EnableLengthMin = false
  JointType = 5 (Distance)
  LengthMax = 0
  LengthMin = 0
  Placement1 = pos=(-3.1e-15,-9e-16,0) rot=(0,0,1;0rad)
  Placement2 = pos=(-63.5,-82.5,62.5) rot=(0.57735,-0.57735,0.57735;2.0944rad)
  Reference1 = -> Assembly [Spacer003.Body.Face4,Spacer003.Body.Vertex3]
  Reference2 = -> Assembly [Stack_Module.Body.Face166,Stack_Module.Body.Vertex404]
FEATURE [App::FeaturePython] Joint010  label="Cylindrical003"  # Assembly joint (typed FeaturePython)
  Activated = true
  AngleMax = 0
  AngleMin = 0
  Detach1 = false
  Detach2 = false
  Distance = 0
  Distance2 = 0
  EnableAngleMax = false
  EnableAngleMin = false
  EnableLengthMax = false
  EnableLengthMin = false
  JointType = 2 (Cylindrical)
  LengthMax = 0
  LengthMin = 0
  Placement1 = pos=(0,0,3.5) rot=(0,0,1;0rad)
  Placement2 = pos=(-63.5,-85,62.5) rot=(0,0.707107,0.707107;3.14159rad)
  Reference1 = -> Assembly [Spacer003.Body.Face1,Spacer003.Body.Face1]
  Reference2 = -> Assembly [Stack_Module.Body.Face159,Stack_Module.Body.Face159]
FEATURE [Assembly::JointGroup] Joints
  Group = -> [GroundedJoint,Joint,Joint001,Joint002,Joint003,Joint004,Joint005,Joint006,Joint007,Joint008,Joint009,Joint010]
FEATURE [Assembly::AssemblyObject] Assembly  label="Assembly_Flight-Cam-Stack"
  Group = -> [Joints,Stack_Module,GroundedJoint,Assembly_Flight_Cam_Screen,Joint,Joint001,Joint002,Spacer,Spacer001,Spacer002,Spacer003,Joint003,Joint004,Joint005,Joint006,Joint007,Joint008,Joint009,Joint010]
  Origin = -> Origin
  Type = Assembly
---- part Assembly_LED-Screen.FCStd = doc fcstd_fb1da1593faa ----
FCSTD DOCUMENT  (FreeCAD 1.0R39319 (Git))
Label: Assembly_LED-Screen
License: All rights reserved
LicenseURL: https://en.wikipedia.org/wiki/All_rights_reserved
objects: App::FeaturePython×6, App::Link×4, Assembly::AssemblyLink×1, Assembly::ViewGroup×1, Assembly::JointGroup×1, Assembly::AssemblyObject×1
EXTERNAL_REF file=../Part/Print/EyeScreen.FCStd obj=Body
EXTERNAL_REF file=Assembly_LED.FCStd obj=Assembly
EXTERNAL_REF file=Assembly_LED.FCStd obj=LED_Eyeball001
EXTERNAL_REF file=Assembly_LED.FCStd obj=LED_Clamp001
EXTERNAL_REF file=../Part/Print/EyeScreen_Clamp.FCStd obj=Body

FEATURE [App::Link] EyeScreen001
  LinkedObject = -> <external ../Part/Print/EyeScreen.FCStd>#Body
FEATURE [App::FeaturePython] GroundedJoint  # Assembly grounded joint (typed FeaturePython)
  ObjectToGround = -> EyeScreen001
FEATURE [App::Link] LED_Eyeball001
  LinkedObject = -> <external Assembly_LED.FCStd>#LED_Eyeball001
FEATURE [App::Link] LED_Clamp001
  LinkPlacement = pos=(3.8e-15,4.1e-15,-13.35) rot=(0,0,-1;0.785398rad)
  LinkedObject = -> <external Assembly_LED.FCStd>#LED_Clamp001
  Placement = pos=(3.8e-15,4.1e-15,-13.35) rot=(0,0,-1;0.785398rad)
FEATURE [Assembly::AssemblyLink] Assembly_LED
  Group = -> [LED_Eyeball001,LED_Clamp001]
  LinkedObject = -> <external Assembly_LED.FCStd>#Assembly
  Origin = -> Origin001
  Placement = pos=(-9.2e-15,0,0) rot=(0.678598,0.281085,0.678598;2.59356rad)
  Rigid = true
FEATURE [App::FeaturePython] Joint  label="Ball"  # Assembly joint (typed FeaturePython)
  Activated = true
  AngleMax = 0
  AngleMin = 0
  Detach1 = false
  Detach2 = false
  Distance = 0
  Distance2 = 0
  EnableAngleMax = false
  EnableAngleMin = false
  EnableLengthMax = false
  EnableLengthMin = false
  JointType = 4 (Ball)
  LengthMax = 0
  LengthMin = 0
  Placement1 = pos=(-9.2e-15,0,0) rot=(0,-1,0;1.5708rad)
  Placement2 = pos=(0,0,0) rot=(1,0,0;3.14159rad)
  Reference1 = -> Assembly [EyeScreen001.Edge48,EyeScreen001.Edge48]
  Reference2 = -> Assembly [Assembly_LED.LED_Eyeball001.Face3,Assembly_LED.LED_Eyeball001.Face3]
FEATURE [App::FeaturePython] Exploded_View  # WARN: FeaturePython — macro-defined, semantics opaque (R4)
FEATURE [Assembly::ViewGroup] Exploded_Views
  Group = -> [Exploded_View]
FEATURE [App::Link] EyeScreen_Clamp001
  LinkPlacement = pos=(-7.29e-14,1.212e-13,7.16e-14) rot=(0,0,1;3.14159rad)
  LinkedObject = -> <external ../Part/Print/EyeScreen_Clamp.FCStd>#Body
  Placement = pos=(-7.29e-14,1.212e-13,7.16e-14) rot=(0,0,1;3.14159rad)
FEATURE [App::FeaturePython] Joint001  label="Distance"  # Assembly joint (typed FeaturePython)
  Activated = true
  AngleMax = 0
  AngleMin = 0
  Detach1 = false
  Detach2 = false
  Distance = -1
  Distance2 = 0
  EnableAngleMax = false
  EnableAngleMin = false
  EnableLengthMax = false
  EnableLengthMin = false
  JointType = 5 (Distance)
  LengthMax = 0
  LengthMin = 0
  Placement1 = pos=(1,-2.048e-13,-1.63309) rot=(-0.707107,0,-0.707107;3.14159rad)
  Placement2 = pos=(4.82e-14,-4.807e-13,-1.66411) rot=(0.707107,0,-0.707107;3.14159rad)
  Reference1 = -> Assembly [EyeScreen_Clamp001.Face3,EyeScreen_Clamp001.Edge9]
  Reference2 = -> Assembly [EyeScreen001.Face105,EyeScreen001.Edge27]
FEATURE [App::FeaturePython] Joint002  label="Distance001"  # Assembly joint (typed FeaturePython)
  Activated = true
  AngleMax = 0
  AngleMin = 0
  Detach1 = false
  Detach2 = false
  Distance = 0
  Distance2 = 0
  EnableAngleMax = false
  EnableAngleMin = false
  EnableLengthMax = false
  EnableLengthMin = false
  JointType = 5 (Distance)
  LengthMax = 0
  LengthMin = 0
  Placement1 = pos=(8.16811,-4.913e-13,-41.75) rot=(0,-1,0;3.14159rad)
  Placement2 = pos=(7.67986,-2.327e-13,-41.75) rot=(0,1,0;3.14159rad)
  Reference1 = -> Assembly [EyeScreen_Clamp001.Face18,EyeScreen_Clamp001.Vertex82]
  Reference2 = -> Assembly [EyeScreen001.Face97,EyeScreen001.Face97]
FEATURE [App::FeaturePython] Joint003  label="Distance002"  # Assembly joint (typed FeaturePython)
  Activated = true
  AngleMax = 0
  AngleMin = 0
  Detach1 = false
  Detach2 = false
  Distance = 0
  Distance2 = 0
  EnableAngleMax = false
  EnableAngleMin = false
  EnableLengthMax = false
  EnableLengthMin = false
  JointType = 5 (Distance)
  LengthMax = 0
  LengthMin = 0
  Placement1 = pos=(5.5,-55,-3.5) rot=(0.57735,-0.57735,0.57735;2.0944rad)
  Placement2 = pos=(5,55,-3.5) rot=(0.57735,-0.57735,0.57735;2.0944rad)
  Reference1 = -> Assembly [EyeScreen_Clamp001.Face8,EyeScreen_Clamp001.Face8]
  Reference2 = -> Assembly [EyeScreen001.Face18,EyeScreen001.Face18]
FEATURE [Assembly::JointGroup] Joints
  Group = -> [GroundedJoint,Joint,Joint001,Joint002,Joint003]
FEATURE [Assembly::AssemblyObject] Assembly  label="Assembly_LED-Screen"
  Group = -> [Joints,EyeScreen001,GroundedJoint,Assembly_LED,Joint,Exploded_Views,Exploded_View,EyeScreen_Clamp001,Joint001,Joint002,Joint003]
  Origin = -> Origin
  Type = Assembly
---- part Assembly_LED-Stack.FCStd = doc fcstd_ecacf25ed709 ----
FCSTD DOCUMENT  (FreeCAD 1.0R39319 (Git))
Label: Assembly_LED-Stack
License: All rights reserved
LicenseURL: https://en.wikipedia.org/wiki/All_rights_reserved
objects: App::FeaturePython×12, App::Link×9, Assembly::AssemblyLink×2, Assembly::JointGroup×1, Assembly::AssemblyObject×1
EXTERNAL_REF file=../Part/Print/Stack_Module.FCStd obj=Body
EXTERNAL_REF file=Assembly_LED-Screen.FCStd obj=Assembly
EXTERNAL_REF file=Assembly_LED-Screen.FCStd obj=EyeScreen001
EXTERNAL_REF file=Assembly_LED-Screen.FCStd obj=Assembly_LED
EXTERNAL_REF file=Assembly_LED.FCStd obj=LED_Eyeball001
EXTERNAL_REF file=Assembly_LED.FCStd obj=LED_Clamp001
EXTERNAL_REF file=Assembly_LED-Screen.FCStd obj=EyeScreen_Clamp001
EXTERNAL_REF file=../Part/Print/Spacer.FCStd obj=Body

FEATURE [App::Link] Stack_Module001
  LinkedObject = -> <external ../Part/Print/Stack_Module.FCStd>#Body
FEATURE [App::FeaturePython] GroundedJoint  # Assembly grounded joint (typed FeaturePython)
  ObjectToGround = -> Stack_Module001
FEATURE [App::Link] EyeScreen001
  LinkedObject = -> <external Assembly_LED-Screen.FCStd>#EyeScreen001
FEATURE [App::Link] LED_Eyeball001
  LinkedObject = -> <external Assembly_LED.FCStd>#LED_Eyeball001
FEATURE [App::Link] LED_Clamp001
  LinkPlacement = pos=(3.8e-15,4.1e-15,-13.35) rot=(0,0,-1;0.785398rad)
  LinkedObject = -> <external Assembly_LED.FCStd>#LED_Clamp001
  Placement = pos=(3.8e-15,4.1e-15,-13.35) rot=(0,0,-1;0.785398rad)
FEATURE [Assembly::AssemblyLink] Assembly_LED
  Group = -> [LED_Eyeball001,LED_Clamp001]
  LinkedObject = -> <external Assembly_LED-Screen.FCStd>#Assembly_LED
  Placement = pos=(-9.2e-15,0,0) rot=(0.678598,0.281085,0.678598;2.59356rad)
  Rigid = true
FEATURE [App::Link] EyeScreen_Clamp001
  LinkPlacement = pos=(-8.42e-14,1.222e-13,2.46e-14) rot=(0,0,1;3.14159rad)
  LinkedObject = -> <external Assembly_LED-Screen.FCStd>#EyeScreen_Clamp001
  Placement = pos=(-8.42e-14,1.222e-13,2.46e-14) rot=(0,0,1;3.14159rad)
FEATURE [Assembly::AssemblyLink] Assembly_LED_Screen  label="Assembly_LED-Screen"
  Group = -> [EyeScreen001,Assembly_LED,EyeScreen_Clamp001]
  LinkedObject = -> <external Assembly_LED-Screen.FCStd>#Assembly
  Origin = -> Origin001
  Placement = pos=(-2.02e-14,-44.75,-20) rot=(0.57735,0.57735,-0.57735;2.0944rad)
  Rigid = true
FEATURE [App::FeaturePython] Joint  label="Distance"  # Assembly joint (typed FeaturePython)
  Activated = true
  AngleMax = 0
  AngleMin = 0
  Detach1 = false
  Detach2 = false
  Distance = 0
  Distance2 = 0
  EnableAngleMax = false
  EnableAngleMin = false
  EnableLengthMax = false
  EnableLengthMin = false
  JointType = 5 (Distance)
  LengthMax = 0
  LengthMin = 0
  Reference1 = -> Assembly [Assembly_LED_Screen.Assembly_LED.LED_Eyeball001.Origin001.,Assembly_LED_Screen.Assembly_LED.LED_Eyeball001.Origin001.]
FEATURE [App::FeaturePython] Joint001  label="Distance001"  # Assembly joint (typed FeaturePython)
  Activated = true
  AngleMax = 0
  AngleMin = 0
  Detach1 = false
  Detach2 = false
  Distance = 0
  Distance2 = 0
  EnableAngleMax = false
  EnableAngleMin = false
  EnableLengthMax = false
  EnableLengthMin = false
  JointType = 5 (Distance)
  LengthMax = 0
  LengthMin = 0
  Placement1 = pos=(7.67986,-2.327e-13,-41.75) rot=(0,1,0;3.14159rad)
  Placement2 = pos=(-4.4e-15,-3,-23.9856) rot=(0.57735,-0.57735,0.57735;2.0944rad)
  Reference1 = -> Assembly [Assembly_LED_Screen.EyeScreen001.Face97,Assembly_LED_Screen.EyeScreen001.Vertex22]
  Reference2 = -> Assembly [Stack_Module001.Face6,Stack_Module001.Vertex68]
FEATURE [App::FeaturePython] Joint002  label="Distance002"  # Assembly joint (typed FeaturePython)
  Activated = true
  AngleMax = 0
  AngleMin = 0
  Detach1 = false
  Detach2 = false
  Distance = -30
  Distance2 = 0
  EnableAngleMax = false
  EnableAngleMin = false
  EnableLengthMax = false
  EnableLengthMin = false
  JointType = 5 (Distance)
  LengthMax = 0
  LengthMin = 0
  Placement1 = pos=(7.6e-15,-40.4281,-60) rot=(0.707107,0.707107,0;3.14159rad)
  Placement2 = pos=(10,-40.7934,-1.63012) rot=(0,-1,0;1.5708rad)
  Reference1 = -> Assembly [Stack_Module001.Face206,Stack_Module001.Vertex218]
  Reference2 = -> Assembly [Assembly_LED_Screen.EyeScreen001.Face2,Assembly_LED_Screen.EyeScreen001.Vertex24]
FEATURE [App::FeaturePython] Joint003  label="Distance003"  # Assembly joint (typed FeaturePython)
  Activated = true
  AngleMax = 0
  AngleMin = 0
  Detach1 = false
  Detach2 = false
  Distance = 1
  Distance2 = 0
  EnableAngleMax = false
  EnableAngleMin = false
  EnableLengthMax = false
  EnableLengthMin = false
  JointType = 5 (Distance)
  LengthMax = 0
  LengthMin = 0
  Placement1 = pos=(56,-43.2991,-15.4982) rot=(-0.707107,0,0.707107;3.14159rad)
  Placement2 = pos=(10,55,-3.5) rot=(0,0,1;0rad)
  Reference1 = -> Assembly [Stack_Module001.Face53,Stack_Module001.Vertex177]
  Reference2 = -> Assembly [Assembly_LED_Screen.EyeScreen001.Edge63,Assembly_LED_Screen.EyeScreen001.Edge63]
FEATURE [App::Link] Spacer001
  LinkPlacement = pos=(63.5,-82.5,62.5) rot=(0.57735,-0.57735,0.57735;2.0944rad)
  LinkedObject = -> <external ../Part/Print/Spacer.FCStd>#Body
  Placement = pos=(63.5,-82.5,62.5) rot=(0.57735,-0.57735,0.57735;2.0944rad)
FEATURE [App::Link] Spacer002
  LinkPlacement = pos=(66.5,-82.5,-53.5) rot=(-0.57735,0.57735,-0.57735;4.18879rad)
  LinkedObject = -> <external ../Part/Print/Spacer.FCStd>#Body
  Placement = pos=(66.5,-82.5,-53.5) rot=(-0.57735,0.57735,-0.57735;4.18879rad)
FEATURE [App::Link] Spacer003
  LinkPlacement = pos=(-66.5,-82.5,-53.5) rot=(-0.57735,0.57735,-0.57735;4.18879rad)
  LinkedObject = -> <external ../Part/Print/Spacer.FCStd>#Body
  Placement = pos=(-66.5,-82.5,-53.5) rot=(-0.57735,0.57735,-0.57735;4.18879rad)
FEATURE [App::Link] Spacer004
  LinkPlacement = pos=(-63.5,-82.5,62.5) rot=(-0.57735,0.57735,-0.57735;4.18879rad)
  LinkedObject = -> <external ../Part/Print/Spacer.FCStd>#Body
  Placement = pos=(-63.5,-82.5,62.5) rot=(-0.57735,0.57735,-0.57735;4.18879rad)
FEATURE [App::FeaturePython] Joint004  label="Distance004"  # Assembly joint (typed FeaturePython)
  Activated = true
  AngleMax = 0
  AngleMin = 0
  Detach1 = false
  Detach2 = false
  Distance = 0
  Distance2 = 0
  EnableAngleMax = false
  EnableAngleMin = false
  EnableLengthMax = false
  EnableLengthMin = false
  JointType = 5 (Distance)
  LengthMax = 0
  LengthMin = 0
  Placement2 = pos=(63.5,-82.5,62.5) rot=(0.57735,0.57735,0.57735;4.18879rad)
  Reference1 = -> Assembly [Spacer001.Face4,Spacer001.Face4]
  Reference2 = -> Assembly [Stack_Module001.Face84,Stack_Module001.Edge2]
FEATURE [App::FeaturePython] Joint005  label="Cylindrical"  # Assembly joint (typed FeaturePython)
  Activated = true
  AngleMax = 0
  AngleMin = 0
  Detach1 = false
  Detach2 = false
  Distance = 0
  Distance2 = 0
  EnableAngleMax = false
  EnableAngleMin = false
  EnableLengthMax = false
  EnableLengthMin = false
  JointType = 2 (Cylindrical)
  LengthMax = 0
  LengthMin = 0
  Placement1 = pos=(0,0,3.5) rot=(0,0,1;0rad)
  Placement2 = pos=(63.5,-85,62.5) rot=(1,0,0;1.5708rad)
  Reference1 = -> Assembly [Spacer001.Face1,Spacer001.Face1]
  Reference2 = -> Assembly [Stack_Module001.Face69,Stack_Module001.Face69]
FEATURE [App::FeaturePython] Joint006  label="Distance005"  # Assembly joint (typed FeaturePython)
  Activated = true
  AngleMax = 0
  AngleMin = 0
  Detach1 = false
  Detach2 = false
  Distance = 0
  Distance2 = 0
  EnableAngleMax = false
  EnableAngleMin = false
  EnableLengthMax = false
  EnableLengthMin = false
  JointType = 5 (Distance)
  LengthMax = 0
  LengthMin = 0
  Placement1 = pos=(-7.1e-15,0,0) rot=(0,0,1;0rad)
  Placement2 = pos=(66.5,-82.5,-53.5) rot=(0.57735,0.57735,0.57735;4.18879rad)
  Reference1 = -> Assembly [Spacer002.Face4,Spacer002.Face4]
  Reference2 = -> Assembly [Stack_Module001.Face80,Stack_Module001.Face80]
FEATURE [App::FeaturePython] Joint007  label="Distance006"  # Assembly joint (typed FeaturePython)
  Activated = true
  AngleMax = 0
  AngleMin = 0
  Detach1 = false
  Detach2 = false
  Distance = 0
  Distance2 = 0
  EnableAngleMax = false
  EnableAngleMin = false
  EnableLengthMax = false
  EnableLengthMin = false
  JointType = 5 (Distance)
  LengthMax = 0
  LengthMin = 0
  Placement1 = pos=(-7.1e-15,0,0) rot=(0,0,1;0rad)
  Placement2 = pos=(-66.5,-82.5,-53.5) rot=(0.57735,-0.57735,0.57735;2.0944rad)
  Reference1 = -> Assembly [Spacer003.Face4,Spacer003.Vertex5]
  Reference2 = -> Assembly [Stack_Module001.Face162,Stack_Module001.Vertex398]
FEATURE [App::FeaturePython] Joint008  label="Cylindrical001"  # Assembly joint (typed FeaturePython)
  Activated = true
  AngleMax = 0
  AngleMin = 0
  Detach1 = false
  Detach2 = false
  Distance = 0
  Distance2 = 0
  EnableAngleMax = false
  EnableAngleMin = false
  EnableLengthMax = false
  EnableLengthMin = false
  JointType = 2 (Cylindrical)
  LengthMax = 0
  LengthMin = 0
  Placement1 = pos=(0,0,3.5) rot=(0,0,1;0rad)
  Placement2 = pos=(-66.5,-87.5,-53.5) rot=(0,0.707107,0.707107;3.14159rad)
  Reference1 = -> Assembly [Spacer003.Face1,Spacer003.Face1]
  Reference2 = -> Assembly [Stack_Module001.Face158,Stack_Module001.Edge2]
FEATURE [App::FeaturePython] Joint009  label="Distance007"  # Assembly joint (typed FeaturePython)
  Activated = true
  AngleMax = 0
  AngleMin = 0
  Detach1 = false
  Detach2 = false
  Distance = 0
  Distance2 = 0
  EnableAngleMax = false
  EnableAngleMin = false
  EnableLengthMax = false
  EnableLengthMin = false
  JointType = 5 (Distance)
  LengthMax = 0
  LengthMin = 0
  Placement1 = pos=(-7.1e-15,0,0) rot=(0,0,1;0rad)
  Placement2 = pos=(-63.5,-82.5,62.5) rot=(0.57735,-0.57735,0.57735;2.0944rad)
  Reference1 = -> Assembly [Spacer004.Face4,Spacer004.Edge1]
  Reference2 = -> Assembly [Stack_Module001.Face166,Stack_Module001.Vertex404]
FEATURE [App::FeaturePython] Joint010  label="Cylindrical002"  # Assembly joint (typed FeaturePython)
  Activated = true
  AngleMax = 0
  AngleMin = 0
  Detach1 = false
  Detach2 = false
  Distance = 0
  Distance2 = 0
  EnableAngleMax = false
  EnableAngleMin = false
  EnableLengthMax = false
  EnableLengthMin = false
  JointType = 2 (Cylindrical)
  LengthMax = 0
  LengthMin = 0
  Placement1 = pos=(0,0,3.5) rot=(0,0,1;0rad)
  Placement2 = pos=(-63.5,-82.5,62.5) rot=(0,0.707107,0.707107;3.14159rad)
  Reference1 = -> Assembly [Spacer004.Face1,Spacer004.Face1]
  Reference2 = -> Assembly [Stack_Module001.Face159,Stack_Module001.Edge3]
FEATURE [Assembly::JointGroup] Joints
  Group = -> [GroundedJoint,Joint,Joint001,Joint002,Joint003,Joint004,Joint005,Joint006,Joint007,Joint008,Joint009,Joint010]
FEATURE [Assembly::AssemblyObject] Assembly  label="Assembly_LED-Stack"
  Group = -> [Joints,Stack_Module001,GroundedJoint,Assembly_LED_Screen,Joint,Joint001,Joint002,Joint003,Spacer001,Spacer002,Spacer003,Spacer004,Joint004,Joint005,Joint006,Joint007,Joint008,Joint009,Joint010]
  Origin = -> Origin
  Type = Assembly
---- part Assembly_PSU-Stack.FCStd = doc fcstd_223338c06e6b ----
FCSTD DOCUMENT  (FreeCAD 1.0R39319 (Git))
Label: Assembly_PSU-Stack
License: All rights reserved
LicenseURL: https://en.wikipedia.org/wiki/All_rights_reserved
objects: App::FeaturePython×22, App::Link×11, Assembly::JointGroup×1, Assembly::AssemblyObject×1
EXTERNAL_REF file=../Part/Print/Stack_Module_PSU.FCStd obj=Part
EXTERNAL_REF file=../Part/Print/Ambient_LED_Screen.FCStd obj=Part
EXTERNAL_REF file=../Part/Print/LinePower_Cover.FCStd obj=Part
EXTERNAL_REF file=../Part/Print/Foot.FCStd obj=Part
EXTERNAL_REF file=../Part/Print/Spacer.FCStd obj=Part

FEATURE [App::Link] Stack_Module_PSU
  LinkedObject = -> <external ../Part/Print/Stack_Module_PSU.FCStd>#Part
FEATURE [App::FeaturePython] GroundedJoint  # Assembly grounded joint (typed FeaturePython)
  ObjectToGround = -> Stack_Module_PSU
FEATURE [App::Link] Ambient_LED_Screen
  LinkPlacement = pos=(-1.22e-14,-3,-62.5) rot=(0,0.707107,-0.707107;3.14159rad)
  LinkedObject = -> <external ../Part/Print/Ambient_LED_Screen.FCStd>#Part
  Placement = pos=(-1.22e-14,-3,-62.5) rot=(0,0.707107,-0.707107;3.14159rad)
FEATURE [App::FeaturePython] Joint  label="Distance"  # Assembly joint (typed FeaturePython)
  Activated = true
  AngleMax = 0
  AngleMin = 0
  Detach1 = false
  Detach2 = false
  Distance = 0
  Distance2 = 0
  EnableAngleMax = false
  EnableAngleMin = false
  EnableLengthMax = false
  EnableLengthMin = false
  JointType = 5 (Distance)
  LengthMax = 0
  LengthMin = 0
  Placement1 = pos=(5.02e-14,1.20274,-3.5e-15) rot=(0,1,0;3.14159rad)
  Placement2 = pos=(-3.81809,-3,-7.3136) rot=(1,0,0;1.5708rad)
  Reference1 = -> Assembly [Ambient_LED_Screen.Body.Face51,Ambient_LED_Screen.Body.Edge30]
  Reference2 = -> Assembly [Stack_Module_PSU.Body.Face1201,Stack_Module_PSU.Body.Edge768]
FEATURE [App::FeaturePython] Joint001  label="Cylindrical"  # Assembly joint (typed FeaturePython)
  Activated = true
  AngleMax = 0
  AngleMin = 0
  Detach1 = false
  Detach2 = false
  Distance = 0
  Distance2 = 0
  EnableAngleMax = false
  EnableAngleMin = false
  EnableLengthMax = false
  EnableLengthMin = false
  JointType = 2 (Cylindrical)
  LengthMax = 0
  LengthMin = 0
  Placement1 = pos=(60.5,3,0) rot=(1,0,0;3.14159rad)
  Placement2 = pos=(-60.5,1.29e-14,-65.5) rot=(0,0.707107,0.707107;3.14159rad)
  Reference1 = -> Assembly [Ambient_LED_Screen.Body.Face52,Ambient_LED_Screen.Body.Edge2]
  Reference2 = -> Assembly [Stack_Module_PSU.Body.Face1184,Stack_Module_PSU.Body.Edge3]
FEATURE [App::FeaturePython] Joint002  label="Cylindrical001"  # Assembly joint (typed FeaturePython)
  Activated = true
  AngleMax = 0
  AngleMin = 0
  Detach1 = false
  Detach2 = false
  Distance = 0
  Distance2 = 0
  EnableAngleMax = false
  EnableAngleMin = false
  EnableLengthMax = false
  EnableLengthMin = false
  JointType = 2 (Cylindrical)
  LengthMax = 0
  LengthMin = 0
  Placement1 = pos=(-60.5,3,-1.34e-14) rot=(0,0,1;3.14159rad)
  Placement2 = pos=(60.5,-1.5,-65.5) rot=(1,0,0;1.5708rad)
  Reference1 = -> Assembly [Ambient_LED_Screen.Body.Face54,Ambient_LED_Screen.Body.Edge2]
  Reference2 = -> Assembly [Stack_Module_PSU.Body.Face1185,Stack_Module_PSU.Body.Face1185]
FEATURE [App::Link] LinePower_Cover
  LinkPlacement = pos=(56,-4,67) rot=(0,-0.707107,0.707107;3.14159rad)
  LinkedObject = -> <external ../Part/Print/LinePower_Cover.FCStd>#Part
  Placement = pos=(56,-4,67) rot=(0,-0.707107,0.707107;3.14159rad)
FEATURE [App::FeaturePython] Joint003  label="Distance001"  # Assembly joint (typed FeaturePython)
  Activated = true
  AngleMax = 0
  AngleMin = 0
  Detach1 = false
  Detach2 = false
  Distance = 0
  Distance2 = 0
  EnableAngleMax = false
  EnableAngleMin = false
  EnableLengthMax = false
  EnableLengthMin = false
  JointType = 5 (Distance)
  LengthMax = 0
  LengthMin = 0
  Placement1 = pos=(42.2837,4.81718,4) rot=(0,0,1;0rad)
  Placement2 = pos=(12.8084,-8,63.1916) rot=(0.57735,0.57735,0.57735;4.18879rad)
  Reference1 = -> Assembly [LinePower_Cover.Body.Face19,LinePower_Cover.Body.Face19]
  Reference2 = -> Assembly [Stack_Module_PSU.Body.Face1235,Stack_Module_PSU.Body.Edge6]
FEATURE [App::FeaturePython] Joint004  label="Cylindrical002"  # Assembly joint (typed FeaturePython)
  Activated = true
  AngleMax = 0
  AngleMin = 0
  Detach1 = false
  Detach2 = false
  Distance = 0
  Distance2 = 0
  EnableAngleMax = false
  EnableAngleMin = false
  EnableLengthMax = false
  EnableLengthMin = false
  JointType = 2 (Cylindrical)
  LengthMax = 0
  LengthMin = 0
  Placement1 = pos=(43,4,5) rot=(0,0,1;0rad)
  Placement2 = pos=(13,-5.5,63) rot=(1,0,0;1.5708rad)
  Reference1 = -> Assembly [LinePower_Cover.Body.Face35,LinePower_Cover.Body.Face35]
  Reference2 = -> Assembly [Stack_Module_PSU.Body.Face1271,Stack_Module_PSU.Body.Face1271]
FEATURE [App::FeaturePython] Joint005  label="Cylindrical003"  # Assembly joint (typed FeaturePython)
  Activated = true
  AngleMax = 0
  AngleMin = 0
  Detach1 = false
  Detach2 = false
  Distance = 0
  Distance2 = 0
  EnableAngleMax = false
  EnableAngleMin = false
  EnableLengthMax = false
  EnableLengthMin = false
  JointType = 2 (Cylindrical)
  LengthMax = 0
  LengthMin = 0
  Placement1 = pos=(3,36,5) rot=(0,0,1;0rad)
  Placement2 = pos=(53,-5.5,31) rot=(1,0,0;1.5708rad)
  Reference1 = -> Assembly [LinePower_Cover.Body.Face36,LinePower_Cover.Body.Face36]
  Reference2 = -> Assembly [Stack_Module_PSU.Body.Face1265,Stack_Module_PSU.Body.Face1265]
FEATURE [App::Link] Foot
  LinkPlacement = pos=(-66.5,5,-53.5) rot=(0.57735,-0.57735,0.57735;2.0944rad)
  LinkedObject = -> <external ../Part/Print/Foot.FCStd>#Part
  Placement = pos=(-66.5,5,-53.5) rot=(0.57735,-0.57735,0.57735;2.0944rad)
FEATURE [App::Link] Foot001
  LinkPlacement = pos=(-63.5,5,62.5) rot=(0.57735,-0.57735,0.57735;2.0944rad)
  LinkedObject = -> <external ../Part/Print/Foot.FCStd>#Part
  Placement = pos=(-63.5,5,62.5) rot=(0.57735,-0.57735,0.57735;2.0944rad)
FEATURE [App::Link] Foot002
  LinkPlacement = pos=(66.5,5,-53.5) rot=(1,0,0;1.5708rad)
  LinkedObject = -> <external ../Part/Print/Foot.FCStd>#Part
  Placement = pos=(66.5,5,-53.5) rot=(1,0,0;1.5708rad)
FEATURE [App::Link] Foot003
  LinkPlacement = pos=(63.5,5,62.5) rot=(0.57735,-0.57735,0.57735;2.0944rad)
  LinkedObject = -> <external ../Part/Print/Foot.FCStd>#Part
  Placement = pos=(63.5,5,62.5) rot=(0.57735,-0.57735,0.57735;2.0944rad)
FEATURE [App::FeaturePython] Joint006  label="Cylindrical004"  # Assembly joint (typed FeaturePython)
  Activated = true
  AngleMax = 0
  AngleMin = 0
  Detach1 = false
  Detach2 = false
  Distance = 0
  Distance2 = 0
  EnableAngleMax = false
  EnableAngleMin = false
  EnableLengthMax = false
  EnableLengthMin = false
  JointType = 2 (Cylindrical)
  LengthMax = 0
  LengthMin = 0
  Placement1 = pos=(0,4e-16,2) rot=(1,0,0;3.14159rad)
  Placement2 = pos=(66.5,-2.5,-53.5) rot=(-1,0,0;1.5708rad)
  Reference1 = -> Assembly [Foot002.Body.Face12,Foot002.Body.Face12]
  Reference2 = -> Assembly [Stack_Module_PSU.Body.Face83,Stack_Module_PSU.Body.Face83]
FEATURE [App::FeaturePython] Joint007  label="Distance002"  # Assembly joint (typed FeaturePython)
  Activated = true
  AngleMax = 0
  AngleMin = 0
  Detach1 = false
  Detach2 = false
  Distance = 0
  Distance2 = 0
  EnableAngleMax = false
  EnableAngleMin = false
  EnableLengthMax = false
  EnableLengthMin = false
  JointType = 5 (Distance)
  LengthMax = 0
  LengthMin = 0
  Placement1 = pos=(9e-16,2.4e-15,5) rot=(0,0,1;3.14159rad)
  Placement2 = pos=(1.08804,3.9e-15,3.01175) rot=(-0.57735,0.57735,0.57735;2.0944rad)
  Reference1 = -> Assembly [Foot002.Body.Face3,Foot002.Body.Face3]
  Reference2 = -> Assembly [Stack_Module_PSU.Body.Face7,Stack_Module_PSU.Body.Vertex102]
FEATURE [App::FeaturePython] Joint008  label="Distance003"  # Assembly joint (typed FeaturePython)
  Activated = true
  AngleMax = 0
  AngleMin = 0
  Detach1 = false
  Detach2 = false
  Distance = 0
  Distance2 = 0
  EnableAngleMax = false
  EnableAngleMin = false
  EnableLengthMax = false
  EnableLengthMin = false
  JointType = 5 (Distance)
  LengthMax = 0
  LengthMin = 0
  Placement1 = pos=(9e-16,2.4e-15,5) rot=(0,0,1;3.14159rad)
  Placement2 = pos=(1.08804,3.9e-15,3.01175) rot=(-0.57735,0.57735,0.57735;2.0944rad)
  Reference1 = -> Assembly [Foot003.Body.Face3,Foot003.Body.Face3]
  Reference2 = -> Assembly [Stack_Module_PSU.Body.Face7,Stack_Module_PSU.Body.Vertex92]
FEATURE [App::FeaturePython] Joint009  label="Cylindrical005"  # Assembly joint (typed FeaturePython)
  Activated = true
  AngleMax = 0
  AngleMin = 0
  Detach1 = false
  Detach2 = false
  Distance = 0
  Distance2 = 0
  EnableAngleMax = false
  EnableAngleMin = false
  EnableLengthMax = false
  EnableLengthMin = false
  JointType = 2 (Cylindrical)
  LengthMax = 0
  LengthMin = 0
  Placement1 = pos=(0,4e-16,2) rot=(1,0,0;3.14159rad)
  Placement2 = pos=(63.5,-2.5,62.5) rot=(-1,0,0;1.5708rad)
  Reference1 = -> Assembly [Foot003.Body.Face12,Foot003.Body.Face12]
  Reference2 = -> Assembly [Stack_Module_PSU.Body.Face82,Stack_Module_PSU.Body.Face82]
FEATURE [App::FeaturePython] Joint010  label="Distance004"  # Assembly joint (typed FeaturePython)
  Activated = true
  AngleMax = 0
  AngleMin = 0
  Detach1 = false
  Detach2 = false
  Distance = 0
  Distance2 = 0
  EnableAngleMax = false
  EnableAngleMin = false
  EnableLengthMax = false
  EnableLengthMin = false
  JointType = 5 (Distance)
  LengthMax = 0
  LengthMin = 0
  Placement1 = pos=(9e-16,2.4e-15,5) rot=(0,0,1;3.14159rad)
  Placement2 = pos=(1.08804,3.9e-15,3.01175) rot=(-0.57735,0.57735,0.57735;2.0944rad)
  Reference1 = -> Assembly [Foot001.Body.Face3,Foot001.Body.Face3]
  Reference2 = -> Assembly [Stack_Module_PSU.Body.Face7,Stack_Module_PSU.Body.Vertex89]
FEATURE [App::FeaturePython] Joint011  label="Cylindrical006"  # Assembly joint (typed FeaturePython)
  Activated = true
  AngleMax = 0
  AngleMin = 0
  Detach1 = false
  Detach2 = false
  Distance = 0
  Distance2 = 0
  EnableAngleMax = false
  EnableAngleMin = false
  EnableLengthMax = false
  EnableLengthMin = false
  JointType = 2 (Cylindrical)
  LengthMax = 0
  LengthMin = 0
  Placement1 = pos=(0,4e-16,2) rot=(1,0,0;3.14159rad)
  Placement2 = pos=(-63.5,-2.5,62.5) rot=(0,0.707107,-0.707107;3.14159rad)
  Reference1 = -> Assembly [Foot001.Body.Face12,Foot001.Body.Face12]
  Reference2 = -> Assembly [Stack_Module_PSU.Body.Face80,Stack_Module_PSU.Body.Face80]
FEATURE [App::FeaturePython] Joint012  label="Distance005"  # Assembly joint (typed FeaturePython)
  Activated = true
  AngleMax = 0
  AngleMin = 0
  Detach1 = false
  Detach2 = false
  Distance = 0
  Distance2 = 0
  EnableAngleMax = false
  EnableAngleMin = false
  EnableLengthMax = false
  EnableLengthMin = false
  JointType = 5 (Distance)
  LengthMax = 0
  LengthMin = 0
  Placement1 = pos=(9e-16,2.4e-15,5) rot=(0,0,1;3.14159rad)
  Placement2 = pos=(1.08804,3.9e-15,3.01175) rot=(-0.57735,0.57735,0.57735;2.0944rad)
  Reference1 = -> Assembly [Foot.Body.Face3,Foot.Body.Face3]
  Reference2 = -> Assembly [Stack_Module_PSU.Body.Face7,Stack_Module_PSU.Body.Edge11]
FEATURE [App::FeaturePython] Joint013  label="Cylindrical007"  # Assembly joint (typed FeaturePython)
  Activated = true
  AngleMax = 0
  AngleMin = 0
  Detach1 = false
  Detach2 = false
  Distance = 0
  Distance2 = 0
  EnableAngleMax = false
  EnableAngleMin = false
  EnableLengthMax = false
  EnableLengthMin = false
  JointType = 2 (Cylindrical)
  LengthMax = 0
  LengthMin = 0
  Placement1 = pos=(0,4e-16,2) rot=(1,0,0;3.14159rad)
  Placement2 = pos=(-66.5,-2.5,-53.5) rot=(0,0.707107,-0.707107;3.14159rad)
  Reference1 = -> Assembly [Foot.Body.Face12,Foot.Body.Face12]
  Reference2 = -> Assembly [Stack_Module_PSU.Body.Face81,Stack_Module_PSU.Body.Face81]
FEATURE [App::Link] Spacer
  LinkPlacement = pos=(66.5,-35.25,-53.5) rot=(-0.57735,0.57735,-0.57735;4.18879rad)
  LinkedObject = -> <external ../Part/Print/Spacer.FCStd>#Part
  Placement = pos=(66.5,-35.25,-53.5) rot=(-0.57735,0.57735,-0.57735;4.18879rad)
FEATURE [App::Link] Spacer001
  LinkPlacement = pos=(63.5,-35.25,62.5) rot=(-0.57735,0.57735,-0.57735;4.18879rad)
  LinkedObject = -> <external ../Part/Print/Spacer.FCStd>#Part
  Placement = pos=(63.5,-35.25,62.5) rot=(-0.57735,0.57735,-0.57735;4.18879rad)
FEATURE [App::Link] Spacer002
  LinkPlacement = pos=(-66.5,-35.25,-53.5) rot=(-0.57735,0.57735,-0.57735;4.18879rad)
  LinkedObject = -> <external ../Part/Print/Spacer.FCStd>#Part
  Placement = pos=(-66.5,-35.25,-53.5) rot=(-0.57735,0.57735,-0.57735;4.18879rad)
FEATURE [App::Link] Spacer003
  LinkPlacement = pos=(-63.5,-35.25,62.5) rot=(0.57735,-0.57735,0.57735;2.0944rad)
  LinkedObject = -> <external ../Part/Print/Spacer.FCStd>#Part
  Placement = pos=(-63.5,-35.25,62.5) rot=(0.57735,-0.57735,0.57735;2.0944rad)
FEATURE [App::FeaturePython] Joint014  label="Distance006"  # Assembly joint (typed FeaturePython)
  Activated = true
  AngleMax = 0
  AngleMin = 0
  Detach1 = false
  Detach2 = false
  Distance = 0
  Distance2 = 0
  EnableAngleMax = false
  EnableAngleMin = false
  EnableLengthMax = false
  EnableLengthMin = false
  JointType = 5 (Distance)
  LengthMax = 0
  LengthMin = 0
  Placement1 = pos=(-3.1e-15,-9e-16,0) rot=(0,0,1;0rad)
  Placement2 = pos=(66.5,-35.25,-53.5) rot=(0.57735,0.57735,0.57735;4.18879rad)
  Reference1 = -> Assembly [Spacer.Body.Face4,Spacer.Body.Face4]
  Reference2 = -> Assembly [Stack_Module_PSU.Body.Face1241,Stack_Module_PSU.Body.Face1241]
FEATURE [App::FeaturePython] Joint015  label="Cylindrical008"  # Assembly joint (typed FeaturePython)
  Activated = true
  AngleMax = 0
  AngleMin = 0
  Detach1 = false
  Detach2 = false
  Distance = 0
  Distance2 = 0
  EnableAngleMax = false
  EnableAngleMin = false
  EnableLengthMax = false
  EnableLengthMin = false
  JointType = 2 (Cylindrical)
  LengthMax = 0
  LengthMin = 0
  Placement1 = pos=(0,0,3.5) rot=(0,0,1;0rad)
  Placement2 = pos=(66.5,-37.75,-53.5) rot=(1,0,0;1.5708rad)
  Reference1 = -> Assembly [Spacer.Body.Face1,Spacer.Body.Face1]
  Reference2 = -> Assembly [Stack_Module_PSU.Body.Face71,Stack_Module_PSU.Body.Face71]
FEATURE [App::FeaturePython] Joint016  label="Distance007"  # Assembly joint (typed FeaturePython)
  Activated = true
  AngleMax = 0
  AngleMin = 0
  Detach1 = false
  Detach2 = false
  Distance = 0
  Distance2 = 0
  EnableAngleMax = false
  EnableAngleMin = false
  EnableLengthMax = false
  EnableLengthMin = false
  JointType = 5 (Distance)
  LengthMax = 0
  LengthMin = 0
  Placement1 = pos=(-3.1e-15,-9e-16,0) rot=(0,0,1;0rad)
  Placement2 = pos=(63.5,-35.25,62.5) rot=(0.57735,0.57735,0.57735;4.18879rad)
  Reference1 = -> Assembly [Spacer001.Body.Face4,Spacer001.Body.Face4]
  Reference2 = -> Assembly [Stack_Module_PSU.Body.Face1240,Stack_Module_PSU.Body.Edge2]
FEATURE [App::FeaturePython] Joint017  label="Distance008"  # Assembly joint (typed FeaturePython)
  Activated = true
  AngleMax = 0
  AngleMin = 0
  Detach1 = false
  Detach2 = false
  Distance = 0
  Distance2 = 0
  EnableAngleMax = false
  EnableAngleMin = false
  EnableLengthMax = false
  EnableLengthMin = false
  JointType = 5 (Distance)
  LengthMax = 0
  LengthMin = 0
  Placement1 = pos=(-3.1e-15,-9e-16,0) rot=(0,0,1;0rad)
  Placement2 = pos=(-66.5,-35.25,-53.5) rot=(0.57735,-0.57735,0.57735;2.0944rad)
  Reference1 = -> Assembly [Spacer002.Body.Face4,Spacer002.Body.Vertex5]
  Reference2 = -> Assembly [Stack_Module_PSU.Body.Face1239,Stack_Module_PSU.Body.Vertex2511]
FEATURE [App::FeaturePython] Joint018  label="Cylindrical009"  # Assembly joint (typed FeaturePython)
  Activated = true
  AngleMax = 0
  AngleMin = 0
  Detach1 = false
  Detach2 = false
  Distance = 0
  Distance2 = 0
  EnableAngleMax = false
  EnableAngleMin = false
  EnableLengthMax = false
  EnableLengthMin = false
  JointType = 2 (Cylindrical)
  LengthMax = 0
  LengthMin = 0
  Placement1 = pos=(0,0,3.5) rot=(0,0,1;0rad)
  Placement2 = pos=(-66.5,-37.75,-53.5) rot=(0,0.707107,0.707107;3.14159rad)
  Reference1 = -> Assembly [Spacer002.Body.Face1,Spacer002.Body.Face1]
  Reference2 = -> Assembly [Stack_Module_PSU.Body.Face69,Stack_Module_PSU.Body.Face69]
FEATURE [App::FeaturePython] Joint019  label="Distance009"  # Assembly joint (typed FeaturePython)
  Activated = true
  AngleMax = 0
  AngleMin = 0
  Detach1 = false
  Detach2 = false
  Distance = 0
  Distance2 = 0
  EnableAngleMax = false
  EnableAngleMin = false
  EnableLengthMax = false
  EnableLengthMin = false
  JointType = 5 (Distance)
  LengthMax = 0
  LengthMin = 0
  Placement1 = pos=(-3.1e-15,-9e-16,0) rot=(0,0,1;0rad)
  Placement2 = pos=(-63.5,-35.25,62.5) rot=(0.57735,-0.57735,0.57735;2.0944rad)
  Reference1 = -> Assembly [Spacer003.Body.Face4,Spacer003.Body.Vertex5]
  Reference2 = -> Assembly [Stack_Module_PSU.Body.Face1238,Stack_Module_PSU.Body.Vertex2510]
FEATURE [App::FeaturePython] Joint020  label="Cylindrical010"  # Assembly joint (typed FeaturePython)
  Activated = true
  AngleMax = 0
  AngleMin = 0
  Detach1 = false
  Detach2 = false
  Distance = 0
  Distance2 = 0
  EnableAngleMax = false
  EnableAngleMin = false
  EnableLengthMax = false
  EnableLengthMin = false
  JointType = 2 (Cylindrical)
  LengthMax = 0
  LengthMin = 0
  Placement1 = pos=(0,0,3.5) rot=(0,0,1;0rad)
  Placement2 = pos=(-63.5,-37.75,62.5) rot=(0,0.707107,0.707107;3.14159rad)
  Reference1 = -> Assembly [Spacer003.Body.Face1,Spacer003.Body.Face1]
  Reference2 = -> Assembly [Stack_Module_PSU.Body.Face68,Stack_Module_PSU.Body.Face68]
FEATURE [Assembly::JointGroup] Joints
  Group = -> [GroundedJoint,Joint,Joint001,Joint002,Joint003,Joint004,Joint005,Joint006,Joint007,Joint008,Joint009,Joint010,Joint011,Joint012,Joint013,Joint014,Joint015,Joint016,Joint017,Joint018,Joint019,Joint020]
FEATURE [Assembly::AssemblyObject] Assembly  label="Assembly_PSU-Stack"
  Group = -> [Joints,Stack_Module_PSU,GroundedJoint,Ambient_LED_Screen,Joint,Joint001,Joint002,LinePower_Cover,Joint003,Joint004,Joint005,Foot,Foot001,Foot002,Foot003,Joint006,Joint007,Joint008,Joint009,Joint010,Joint011,Joint012,Joint013,Spacer,Spacer001,Spacer002,Spacer003,Joint014,Joint015,Joint016,Joint017,Joint018,Joint019,Joint020]
  Origin = -> Origin
  Type = Assembly
---- part Assembly_Tee-Cam-Screen.FCStd = doc fcstd_f5825ac490de ----
FCSTD DOCUMENT  (FreeCAD 1.0R39319 (Git))
Label: Assembly_Tee-Cam-Screen
License: All rights reserved
LicenseURL: https://en.wikipedia.org/wiki/All_rights_reserved
objects: App::FeaturePython×5, App::Link×3, Assembly::AssemblyLink×1, Assembly::JointGroup×1, Assembly::AssemblyObject×1
EXTERNAL_REF file=../Part/Print/EyeScreen.FCStd obj=Part
EXTERNAL_REF file=../Part/Print/EyeScreen_Clamp.FCStd obj=Part
EXTERNAL_REF file=Assembly_Tee-Cam.FCStd obj=Assembly
EXTERNAL_REF file=Assembly_Tee-Cam.FCStd obj=IMX296_MPI_Eyeball_6mm001

FEATURE [App::Link] EyeScreen
  LinkPlacement = pos=(0,0,0) rot=(0,0,1;3.14159rad)
  LinkedObject = -> <external ../Part/Print/EyeScreen.FCStd>#Part
  Placement = pos=(0,0,0) rot=(0,0,1;3.14159rad)
FEATURE [App::Link] EyeScreen_Clamp
  LinkPlacement = pos=(7.31e-14,1.385e-13,-2.516e-13) rot=(0,0,1;0rad)
  LinkedObject = -> <external ../Part/Print/EyeScreen_Clamp.FCStd>#Part
  Placement = pos=(7.31e-14,1.385e-13,-2.516e-13) rot=(0,0,1;0rad)
FEATURE [App::FeaturePython] GroundedJoint  # Assembly grounded joint (typed FeaturePython)
  ObjectToGround = -> EyeScreen
  Placement = pos=(0,0,0) rot=(0,0,1;3.14159rad)
FEATURE [App::FeaturePython] Joint  label="Distance"  # Assembly joint (typed FeaturePython)
  Activated = true
  AngleMax = 0
  AngleMin = 0
  Detach1 = false
  Detach2 = false
  Distance = -1
  Distance2 = 0
  EnableAngleMax = false
  EnableAngleMin = false
  EnableLengthMax = false
  EnableLengthMin = false
  JointType = 5 (Distance)
  LengthMax = 0
  LengthMin = 0
  Placement1 = pos=(1,-2.077e-13,-1.63309) rot=(0.707107,0,0.707107;3.14159rad)
  Placement2 = pos=(4.82e-14,-4.807e-13,-1.66411) rot=(0.707107,0,-0.707107;3.14159rad)
  Reference1 = -> Assembly [EyeScreen_Clamp.Body.Face3,EyeScreen_Clamp.Body.Edge29]
  Reference2 = -> Assembly [EyeScreen.Body.Face105,EyeScreen.Body.Vertex111]
FEATURE [App::FeaturePython] Joint001  label="Cylindrical"  # Assembly joint (typed FeaturePython)
  Activated = true
  AngleMax = 0
  AngleMin = 0
  Detach1 = false
  Detach2 = false
  Distance = 0
  Distance2 = 0
  EnableAngleMax = false
  EnableAngleMin = false
  EnableLengthMax = false
  EnableLengthMin = false
  JointType = 2 (Cylindrical)
  LengthMax = 0
  LengthMin = 0
  Placement1 = pos=(3,-43.3013,25) rot=(0.57735,-0.57735,-0.57735;2.0944rad)
  Placement2 = pos=(5,43.3013,25) rot=(0.57735,0.57735,0.57735;2.0944rad)
  Reference1 = -> Assembly [EyeScreen_Clamp.Body.Face32,EyeScreen_Clamp.Body.Face32]
  Reference2 = -> Assembly [EyeScreen.Body.Face28,EyeScreen.Body.Face28]
FEATURE [App::FeaturePython] Joint002  label="Cylindrical001"  # Assembly joint (typed FeaturePython)
  Activated = true
  AngleMax = 0
  AngleMin = 0
  Detach1 = false
  Detach2 = false
  Distance = 0
  Distance2 = 0
  EnableAngleMax = false
  EnableAngleMin = false
  EnableLengthMax = false
  EnableLengthMin = false
  JointType = 2 (Cylindrical)
  LengthMax = 0
  LengthMin = 0
  Placement1 = pos=(3,-43.3013,-25) rot=(0.57735,-0.57735,0.57735;4.18879rad)
  Placement2 = pos=(5,43.3013,-25) rot=(0.57735,0.57735,-0.57735;4.18879rad)
  Reference1 = -> Assembly [EyeScreen_Clamp.Body.Face31,EyeScreen_Clamp.Body.Face31]
  Reference2 = -> Assembly [EyeScreen.Body.Face29,EyeScreen.Body.Face29]
FEATURE [App::Link] IMX296_MPI_Eyeball_6mm001  label="IMX296-MPI_Eyeball_6mm001"
  LinkedObject = -> <external Assembly_Tee-Cam.FCStd>#IMX296_MPI_Eyeball_6mm001
FEATURE [Assembly::AssemblyLink] Assembly_Tee_Cam  label="Assembly_Tee-Cam"
  Group = -> [IMX296_MPI_Eyeball_6mm001]
  LinkedObject = -> <external Assembly_Tee-Cam.FCStd>#Assembly
  Origin = -> Origin001
  Placement = pos=(9.2e-15,0,0) rot=(0.57735,0.57735,-0.57735;4.18879rad)
  Rigid = true
FEATURE [App::FeaturePython] Joint003  label="Ball"  # Assembly joint (typed FeaturePython)
  Activated = true
  AngleMax = 0
  AngleMin = 0
  Detach1 = false
  Detach2 = false
  Distance = 0
  Distance2 = 0
  EnableAngleMax = false
  EnableAngleMin = false
  EnableLengthMax = false
  EnableLengthMin = false
  JointType = 4 (Ball)
  LengthMax = 0
  LengthMin = 0
  Placement1 = pos=(0,0,0) rot=(1,0,0;3.14159rad)
  Placement2 = pos=(-9.2e-15,0,0) rot=(0.707107,0,0.707107;3.14159rad)
  Reference1 = -> Assembly [Assembly_Tee_Cam.IMX296_MPI_Eyeball_6mm001.Face1,Assembly_Tee_Cam.IMX296_MPI_Eyeball_6mm001.Face1]
  Reference2 = -> Assembly [EyeScreen.Body.Edge142,EyeScreen.Body.Edge142]
FEATURE [Assembly::JointGroup] Joints
  Group = -> [GroundedJoint,Joint,Joint001,Joint002,Joint003]
FEATURE [Assembly::AssemblyObject] Assembly  label="Assembly_Tee-Cam-Screen"
  Group = -> [Joints,EyeScreen,EyeScreen_Clamp,GroundedJoint,Joint,Joint001,Joint002,Assembly_Tee_Cam,Joint003]
  Origin = -> Origin
  Type = Assembly_Flight-Cam-Screen
---- part Assembly_Tee-Cam-Stack.FCStd = doc fcstd_4e22d7623b17 ----
FCSTD DOCUMENT  (FreeCAD 1.0R39319 (Git))
Label: Assembly_Tee-Cam-Stack
License: All rights reserved
LicenseURL: https://en.wikipedia.org/wiki/All_rights_reserved
objects: App::FeaturePython×12, App::Link×8, Assembly::AssemblyLink×2, Assembly::JointGroup×1, Assembly::AssemblyObject×1
EXTERNAL_REF file=../Part/Print/Stack_Module.FCStd obj=Part
EXTERNAL_REF file=../Part/Print/Spacer.FCStd obj=Part
EXTERNAL_REF file=Assembly_Tee-Cam-Screen.FCStd obj=Assembly
EXTERNAL_REF file=Assembly_Tee-Cam-Screen.FCStd obj=EyeScreen
EXTERNAL_REF file=Assembly_Tee-Cam-Screen.FCStd obj=EyeScreen_Clamp
EXTERNAL_REF file=Assembly_Tee-Cam-Screen.FCStd obj=Assembly_Tee_Cam
EXTERNAL_REF file=Assembly_Tee-Cam.FCStd obj=IMX296_MPI_Eyeball_6mm001

FEATURE [App::Link] Stack_Module
  LinkedObject = -> <external ../Part/Print/Stack_Module.FCStd>#Part
FEATURE [App::FeaturePython] GroundedJoint  # Assembly grounded joint (typed FeaturePython)
  ObjectToGround = -> Stack_Module
FEATURE [App::Link] Spacer
  LinkPlacement = pos=(-66.5,-82.5,-53.5) rot=(-0.57735,0.57735,-0.57735;4.18879rad)
  LinkedObject = -> <external ../Part/Print/Spacer.FCStd>#Part
  Placement = pos=(-66.5,-82.5,-53.5) rot=(-0.57735,0.57735,-0.57735;4.18879rad)
FEATURE [App::Link] Spacer001
  LinkPlacement = pos=(63.5,-82.5,62.5) rot=(0.57735,-0.57735,0.57735;2.0944rad)
  LinkedObject = -> <external ../Part/Print/Spacer.FCStd>#Part
  Placement = pos=(63.5,-82.5,62.5) rot=(0.57735,-0.57735,0.57735;2.0944rad)
FEATURE [App::Link] Spacer002
  LinkPlacement = pos=(66.5,-82.5,-53.5) rot=(0.57735,-0.57735,0.57735;2.0944rad)
  LinkedObject = -> <external ../Part/Print/Spacer.FCStd>#Part
  Placement = pos=(66.5,-82.5,-53.5) rot=(0.57735,-0.57735,0.57735;2.0944rad)
FEATURE [App::Link] Spacer003
  LinkPlacement = pos=(-63.5,-82.5,62.5) rot=(-0.57735,0.57735,-0.57735;4.18879rad)
  LinkedObject = -> <external ../Part/Print/Spacer.FCStd>#Part
  Placement = pos=(-63.5,-82.5,62.5) rot=(-0.57735,0.57735,-0.57735;4.18879rad)
FEATURE [App::FeaturePython] Joint003  label="Distance003"  # Assembly joint (typed FeaturePython)
  Activated = true
  AngleMax = 0
  AngleMin = 0
  Detach1 = false
  Detach2 = false
  Distance = 0
  Distance2 = 0
  EnableAngleMax = false
  EnableAngleMin = false
  EnableLengthMax = false
  EnableLengthMin = false
  JointType = 5 (Distance)
  LengthMax = 0
  LengthMin = 0
  Placement1 = pos=(-3.1e-15,-9e-16,0) rot=(0,0,1;0rad)
  Placement2 = pos=(63.5,-82.5,62.5) rot=(0.57735,0.57735,0.57735;4.18879rad)
  Reference1 = -> Assembly [Spacer001.Body.Face4,Spacer001.Body.Face4]
  Reference2 = -> Assembly [Stack_Module.Body.Face84,Stack_Module.Body.Edge2]
FEATURE [App::FeaturePython] Joint004  label="Cylindrical"  # Assembly joint (typed FeaturePython)
  Activated = true
  AngleMax = 0
  AngleMin = 0
  Detach1 = false
  Detach2 = false
  Distance = 0
  Distance2 = 0
  EnableAngleMax = false
  EnableAngleMin = false
  EnableLengthMax = false
  EnableLengthMin = false
  JointType = 2 (Cylindrical)
  LengthMax = 0
  LengthMin = 0
  Placement1 = pos=(0,0,3.5) rot=(0,0,1;0rad)
  Placement2 = pos=(63.5,-85,62.5) rot=(1,0,0;1.5708rad)
  Reference1 = -> Assembly [Spacer001.Body.Face1,Spacer001.Body.Face1]
  Reference2 = -> Assembly [Stack_Module.Body.Face69,Stack_Module.Body.Face69]
FEATURE [App::FeaturePython] Joint005  label="Distance004"  # Assembly joint (typed FeaturePython)
  Activated = true
  AngleMax = 0
  AngleMin = 0
  Detach1 = false
  Detach2 = false
  Distance = 0
  Distance2 = 0
  EnableAngleMax = false
  EnableAngleMin = false
  EnableLengthMax = false
  EnableLengthMin = false
  JointType = 5 (Distance)
  LengthMax = 0
  LengthMin = 0
  Placement1 = pos=(-3.1e-15,-9e-16,0) rot=(0,0,1;0rad)
  Placement2 = pos=(66.5,-82.5,-53.5) rot=(0.57735,0.57735,0.57735;4.18879rad)
  Reference1 = -> Assembly [Spacer002.Body.Face4,Spacer002.Body.Face4]
  Reference2 = -> Assembly [Stack_Module.Body.Face80,Stack_Module.Body.Edge2]
FEATURE [App::FeaturePython] Joint006  label="Cylindrical001"  # Assembly joint (typed FeaturePython)
  Activated = true
  AngleMax = 0
  AngleMin = 0
  Detach1 = false
  Detach2 = false
  Distance = 0
  Distance2 = 0
  EnableAngleMax = false
  EnableAngleMin = false
  EnableLengthMax = false
  EnableLengthMin = false
  JointType = 2 (Cylindrical)
  LengthMax = 0
  LengthMin = 0
  Placement1 = pos=(0,0,3.5) rot=(0,0,1;0rad)
  Placement2 = pos=(66.5,-85,-53.5) rot=(1,0,0;1.5708rad)
  Reference1 = -> Assembly [Spacer002.Body.Face1,Spacer002.Body.Face1]
  Reference2 = -> Assembly [Stack_Module.Body.Face68,Stack_Module.Body.Face68]
FEATURE [App::FeaturePython] Joint007  label="Distance005"  # Assembly joint (typed FeaturePython)
  Activated = true
  AngleMax = 0
  AngleMin = 0
  Detach1 = false
  Detach2 = false
  Distance = 0
  Distance2 = 0
  EnableAngleMax = false
  EnableAngleMin = false
  EnableLengthMax = false
  EnableLengthMin = false
  JointType = 5 (Distance)
  LengthMax = 0
  LengthMin = 0
  Placement1 = pos=(-3.1e-15,-9e-16,0) rot=(0,0,1;0rad)
  Placement2 = pos=(-66.5,-82.5,-53.5) rot=(0.57735,-0.57735,0.57735;2.0944rad)
  Reference1 = -> Assembly [Spacer.Body.Face4,Spacer.Body.Vertex5]
  Reference2 = -> Assembly [Stack_Module.Body.Face162,Stack_Module.Body.Edge2]
FEATURE [App::FeaturePython] Joint008  label="Cylindrical002"  # Assembly joint (typed FeaturePython)
  Activated = true
  AngleMax = 0
  AngleMin = 0
  Detach1 = false
  Detach2 = false
  Distance = 0
  Distance2 = 0
  EnableAngleMax = false
  EnableAngleMin = false
  EnableLengthMax = false
  EnableLengthMin = false
  JointType = 2 (Cylindrical)
  LengthMax = 0
  LengthMin = 0
  Placement1 = pos=(0,0,3.5) rot=(0,0,1;0rad)
  Placement2 = pos=(-66.5,-85,-53.5) rot=(0,0.707107,0.707107;3.14159rad)
  Reference1 = -> Assembly [Spacer.Body.Face1,Spacer.Body.Face1]
  Reference2 = -> Assembly [Stack_Module.Body.Face158,Stack_Module.Body.Face158]
FEATURE [App::FeaturePython] Joint009  label="Distance006"  # Assembly joint (typed FeaturePython)
  Activated = true
  AngleMax = 0
  AngleMin = 0
  Detach1 = false
  Detach2 = false
  Distance = 0
  Distance2 = 0
  EnableAngleMax = false
  EnableAngleMin = false
  EnableLengthMax = false
  EnableLengthMin = false
  JointType = 5 (Distance)
  LengthMax = 0
  LengthMin = 0
  Placement1 = pos=(-3.1e-15,-9e-16,0) rot=(0,0,1;0rad)
  Placement2 = pos=(-63.5,-82.5,62.5) rot=(0.57735,-0.57735,0.57735;2.0944rad)
  Reference1 = -> Assembly [Spacer003.Body.Face4,Spacer003.Body.Vertex3]
  Reference2 = -> Assembly [Stack_Module.Body.Face166,Stack_Module.Body.Vertex404]
FEATURE [App::FeaturePython] Joint010  label="Cylindrical003"  # Assembly joint (typed FeaturePython)
  Activated = true
  AngleMax = 0
  AngleMin = 0
  Detach1 = false
  Detach2 = false
  Distance = 0
  Distance2 = 0
  EnableAngleMax = false
  EnableAngleMin = false
  EnableLengthMax = false
  EnableLengthMin = false
  JointType = 2 (Cylindrical)
  LengthMax = 0
  LengthMin = 0
  Placement1 = pos=(0,0,3.5) rot=(0,0,1;0rad)
  Placement2 = pos=(-63.5,-85,62.5) rot=(0,0.707107,0.707107;3.14159rad)
  Reference1 = -> Assembly [Spacer003.Body.Face1,Spacer003.Body.Face1]
  Reference2 = -> Assembly [Stack_Module.Body.Face159,Stack_Module.Body.Face159]
FEATURE [App::Link] EyeScreen
  LinkPlacement = pos=(0,0,0) rot=(0,0,1;3.14159rad)
  LinkedObject = -> <external Assembly_Tee-Cam-Screen.FCStd>#EyeScreen
  Placement = pos=(0,0,0) rot=(0,0,1;3.14159rad)
FEATURE [App::Link] EyeScreen_Clamp
  LinkPlacement = pos=(6.2e-14,1.473e-13,-3.4e-13) rot=(0,0,1;0rad)
  LinkedObject = -> <external Assembly_Tee-Cam-Screen.FCStd>#EyeScreen_Clamp
  Placement = pos=(6.2e-14,1.473e-13,-3.4e-13) rot=(0,0,1;0rad)
FEATURE [App::Link] IMX296_MPI_Eyeball_6mm001  label="IMX296-MPI_Eyeball_6mm001"
  LinkedObject = -> <external Assembly_Tee-Cam.FCStd>#IMX296_MPI_Eyeball_6mm001
FEATURE [Assembly::AssemblyLink] Assembly_Tee_Cam  label="Assembly_Tee-Cam"
  Group = -> [IMX296_MPI_Eyeball_6mm001]
  LinkedObject = -> <external Assembly_Tee-Cam-Screen.FCStd>#Assembly_Tee_Cam
  Placement = pos=(9.2e-15,0,0) rot=(0.57735,0.57735,-0.57735;4.18879rad)
  Rigid = true
FEATURE [Assembly::AssemblyLink] Assembly_Tee_Cam_Screen  label="Assembly_Tee-Cam-Screen"
  Group = -> [EyeScreen,EyeScreen_Clamp,Assembly_Tee_Cam]
  LinkedObject = -> <external Assembly_Tee-Cam-Screen.FCStd>#Assembly
  Origin = -> Origin001
  Placement = pos=(1,-44.75,-20) rot=(-0.57735,0.57735,-0.57735;4.18879rad)
  Rigid = true
FEATURE [App::FeaturePython] Joint  label="Distance"  # Assembly joint (typed FeaturePython)
  Activated = true
  AngleMax = 0
  AngleMin = 0
  Detach1 = false
  Detach2 = false
  Distance = 0
  Distance2 = 0
  EnableAngleMax = false
  EnableAngleMin = false
  EnableLengthMax = false
  EnableLengthMin = false
  JointType = 5 (Distance)
  LengthMax = 0
  LengthMin = 0
  Placement1 = pos=(7.67986,-2.327e-13,-41.75) rot=(0,1,0;3.14159rad)
  Placement2 = pos=(-4.4e-15,-3,-23.9856) rot=(0.57735,-0.57735,0.57735;2.0944rad)
  Reference1 = -> Assembly [Assembly_Tee_Cam_Screen.EyeScreen.Body.Face97,Assembly_Tee_Cam_Screen.EyeScreen.Body.Vertex133]
  Reference2 = -> Assembly [Stack_Module.Body.Face6,Stack_Module.Body.Vertex32]
FEATURE [App::FeaturePython] Joint011  label="Distance007"  # Assembly joint (typed FeaturePython)
  Activated = true
  AngleMax = 0
  AngleMin = 0
  Detach1 = false
  Detach2 = false
  Distance = -30
  Distance2 = 0
  EnableAngleMax = false
  EnableAngleMin = false
  EnableLengthMax = false
  EnableLengthMin = false
  JointType = 5 (Distance)
  LengthMax = 0
  LengthMin = 0
  Placement1 = pos=(10,-40.7934,-1.63012) rot=(0,-1,0;1.5708rad)
  Placement2 = pos=(7.6e-15,-40.4281,-60) rot=(0.707107,0.707107,0;3.14159rad)
  Reference1 = -> Assembly [Assembly_Tee_Cam_Screen.EyeScreen.Body.Face2,Assembly_Tee_Cam_Screen.EyeScreen.Body.Edge30]
  Reference2 = -> Assembly [Stack_Module.Body.Face206,Stack_Module.Body.Vertex20]
FEATURE [App::FeaturePython] Joint012  label="Distance008"  # Assembly joint (typed FeaturePython)
  Activated = true
  AngleMax = 0
  AngleMin = 0
  Detach1 = false
  Detach2 = false
  Distance = 0
  Distance2 = 0
  EnableAngleMax = false
  EnableAngleMin = false
  EnableLengthMax = false
  EnableLengthMin = false
  JointType = 5 (Distance)
  LengthMax = 0
  LengthMin = 0
  Placement1 = pos=(56,-43.2991,-15.4982) rot=(-0.707107,0,0.707107;3.14159rad)
  Placement2 = pos=(10,55,-3.5) rot=(0,0,1;0rad)
  Reference1 = -> Assembly [Stack_Module.Body.Face53,Stack_Module.Body.Vertex177]
  Reference2 = -> Assembly [Assembly_Tee_Cam_Screen.EyeScreen.Body.Edge63,Assembly_Tee_Cam_Screen.EyeScreen.Body.Edge63]
FEATURE [Assembly::JointGroup] Joints
  Group = -> [GroundedJoint,Joint003,Joint004,Joint005,Joint006,Joint007,Joint008,Joint009,Joint010,Joint,Joint011,Joint012]
FEATURE [Assembly::AssemblyObject] Assembly  label="Assembly_Tee-Cam-Stack"
  Group = -> [Joints,Stack_Module,GroundedJoint,Spacer,Spacer001,Spacer002,Spacer003,Joint003,Joint004,Joint005,Joint006,Joint007,Joint008,Joint009,Joint010,Assembly_Tee_Cam_Screen,Joint,Joint011,Joint012]
  Origin = -> Origin
  Type = Assembly
